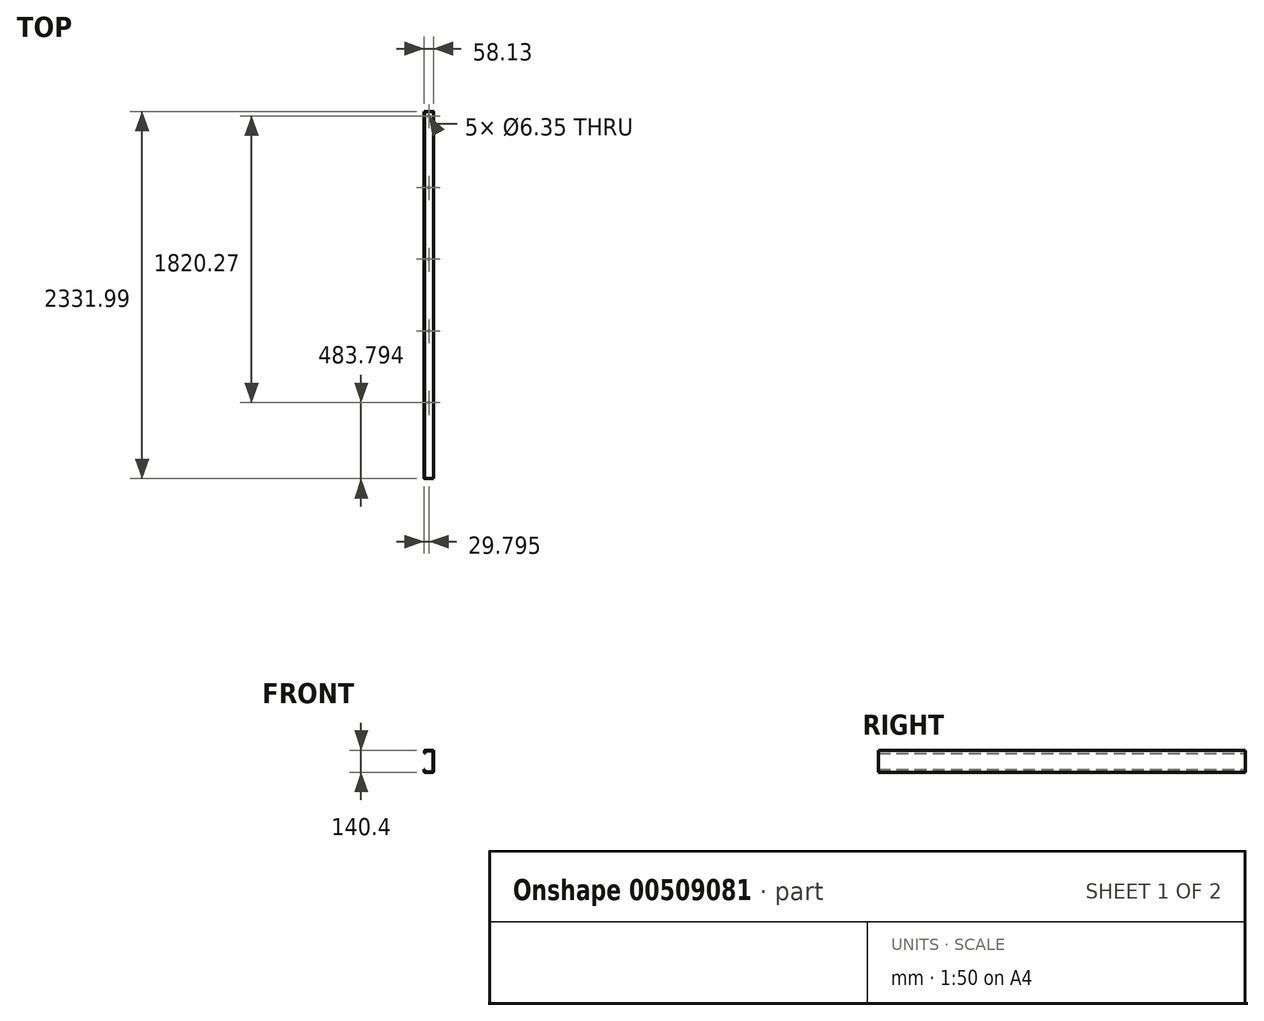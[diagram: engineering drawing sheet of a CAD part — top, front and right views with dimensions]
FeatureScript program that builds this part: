
annotation { "Feature Type Name" : "Feature", "Feature Type Description" : "" }
export const myFeature = defineFeature(function(context is Context, id is Id, definition is map)
    precondition{}
    {
        {
            var Q0;
            Q0=qCreatedBy(makeId("Front.planeOp"),FACE);
            var sketch = newSketch(context, id + "F0", { "sketchPlane" : qUnion([Q0])});
            skLineSegment(sketch, "E0", {"start": v(-431.8, -558.8) * mm, "end": v(431.8, -558.8) * mm});
            skLineSegment(sketch, "E1", {"start": v(431.8, -558.8) * mm, "end": v(431.8, 558.8) * mm});
            skLineSegment(sketch, "E2", {"start": v(431.8, 558.8) * mm, "end": v(-431.8, 558.8) * mm});
            skLineSegment(sketch, "E3", {"start": v(-431.8, 558.8) * mm, "end": v(-431.8, -558.8) * mm});
            skLineSegment(sketch, "E4", {"start": v(-381, -504.83) * mm, "end": v(381, -504.83) * mm});
            skLineSegment(sketch, "E5", {"start": v(381, -504.83) * mm, "end": v(381, 504.83) * mm});
            skLineSegment(sketch, "E6", {"start": v(381, 504.83) * mm, "end": v(360.7, 504.83) * mm});
            skLineSegment(sketch, "E7", {"start": v(265.82, 504.83) * mm, "end": v(-381, 504.83) * mm});
            skLineSegment(sketch, "E8", {"start": v(-381, 504.83) * mm, "end": v(-381, -504.83) * mm});
            skLineSegment(sketch, "E9", {"start": v(-381, -403.23) * mm, "end": v(381, -403.23) * mm});
            skLineSegment(sketch, "E10", {"start": v(-152.4, -403.23) * mm, "end": v(-152.4, -504.83) * mm});
            skLineSegment(sketch, "E11", {"start": v(152.4, -403.23) * mm, "end": v(152.4, -504.83) * mm});
            skLineSegment(sketch, "E12", {"start": v(349.12, 503.33) * mm, "end": v(324.77, 544.8) * mm});
            skLineSegment(sketch, "E13", {"start": v(324.92, 525.17) * mm, "end": v(343.26, 493.25) * mm});
            skLineSegment(sketch, "E14", {"start": v(345.3, 496.77) * mm, "end": v(323.11, 534.57) * mm});
            skLineSegment(sketch, "E15", {"start": v(351.17, 506.85) * mm, "end": v(327.06, 548.5) * mm});
            skLineSegment(sketch, "E16", {"start": v(335.24, 486.66) * mm, "end": v(339.43, 486.66) * mm});
            skLineSegment(sketch, "E17", {"start": v(323.53, 514.34) * mm, "end": v(339.43, 486.66) * mm});
            skLineSegment(sketch, "E18", {"start": v(324.77, 544.8) * mm, "end": v(303.2, 507.27) * mm});
            skLineSegment(sketch, "E19", {"start": v(323.11, 534.57) * mm, "end": v(305.2, 503.47) * mm});
            skLineSegment(sketch, "E20", {"start": v(303.02, 548.5) * mm, "end": v(279.32, 507.27) * mm});
            skLineSegment(sketch, "E21", {"start": v(305.2, 503.47) * mm, "end": v(281.51, 503.47) * mm});
            skLineSegment(sketch, "E22", {"start": v(303.2, 507.27) * mm, "end": v(279.32, 507.27) * mm});
            skLineSegment(sketch, "E23", {"start": v(287.46, 493.17) * mm, "end": v(311.53, 493.17) * mm});
            skLineSegment(sketch, "E24", {"start": v(285.48, 496.6) * mm, "end": v(309, 496.6) * mm});
            skLineSegment(sketch, "E25", {"start": v(315.3, 486.66) * mm, "end": v(291.22, 486.66) * mm});
            skLineSegment(sketch, "E26", {"start": v(281.51, 503.47) * mm, "end": v(285.48, 496.6) * mm});
            skLineSegment(sketch, "E27", {"start": v(287.46, 493.17) * mm, "end": v(291.22, 486.66) * mm});
            skLineSegment(sketch, "E28", {"start": v(309, 496.6) * mm, "end": v(324.92, 525.17) * mm});
            skLineSegment(sketch, "E29", {"start": v(311.53, 493.17) * mm, "end": v(323.53, 514.34) * mm});
            skLineSegment(sketch, "E30", {"start": v(325.28, 503.65) * mm, "end": v(315.3, 486.66) * mm});
            skLineSegment(sketch, "E31", {"start": v(319.7, 486.66) * mm, "end": v(326.89, 486.66) * mm});
            skLineSegment(sketch, "E32", {"start": v(319.7, 486.66) * mm, "end": v(323.3, 492.99) * mm});
            skLineSegment(sketch, "E33", {"start": v(335.24, 486.66) * mm, "end": v(325.28, 503.65) * mm});
            skLineSegment(sketch, "E34", {"start": v(323.3, 492.99) * mm, "end": v(326.89, 486.66) * mm});
            skLineSegment(sketch, "E35", {"start": v(327.06, 548.5) * mm, "end": v(303.02, 548.5) * mm});
            skLineSegment(sketch, "E36", {"start": v(343.26, 493.25) * mm, "end": v(345.3, 496.77) * mm});
            skLineSegment(sketch, "E37", {"start": v(349.12, 503.33) * mm, "end": v(351.17, 506.85) * mm});
            skCircle(sketch, "E38", {"center": v(350.6, 458.79) * mm, "radius": 1.85 * mm});
            skLineSegment(sketch, "E39", {"start": v(-201.65, 389.86) * mm, "end": v(-204.7, 389.86) * mm});
            skLineSegment(sketch, "E40", {"start": v(-201.65, 287.56) * mm, "end": v(-204.7, 287.56) * mm});
            skLineSegment(sketch, "E41", {"start": v(-204.7, 389.86) * mm, "end": v(-204.7, 405.1) * mm});
            skLineSegment(sketch, "E42", {"start": v(-201.65, 389.86) * mm, "end": v(-201.65, 405.1) * mm});
            skArc(sketch, "E43", {"start": v(-200.89, 405.86) * mm, "mid": v(-201.43, 405.64) * mm, "end": v(-201.65, 405.1) * mm});
            skArc(sketch, "E44", {"start": v(-200.89, 408.9) * mm, "mid": v(-203.58, 407.8) * mm, "end": v(-204.7, 405.1) * mm});
            skLineSegment(sketch, "E45", {"start": v(-200.89, 408.9) * mm, "end": v(-151.83, 408.9) * mm});
            skLineSegment(sketch, "E46", {"start": v(-200.89, 405.86) * mm, "end": v(-151.83, 405.86) * mm});
            skArc(sketch, "E47", {"start": v(-151.07, 405.1) * mm, "mid": v(-151.3, 405.64) * mm, "end": v(-151.83, 405.86) * mm});
            skArc(sketch, "E48", {"start": v(-148.02, 405.1) * mm, "mid": v(-149.14, 407.8) * mm, "end": v(-151.83, 408.9) * mm});
            skLineSegment(sketch, "E49", {"start": v(-148.02, 405.1) * mm, "end": v(-148.02, 272.32) * mm});
            skLineSegment(sketch, "E50", {"start": v(-151.07, 405.1) * mm, "end": v(-151.07, 272.32) * mm});
            skLineSegment(sketch, "E51", {"start": v(-204.7, 287.56) * mm, "end": v(-204.7, 273.15) * mm});
            skLineSegment(sketch, "E52", {"start": v(-201.65, 287.56) * mm, "end": v(-201.65, 273.15) * mm});
            skLineSegment(sketch, "E53", {"start": v(-200.06, 268.51) * mm, "end": v(-151.83, 268.51) * mm});
            skLineSegment(sketch, "E54", {"start": v(-200.06, 271.56) * mm, "end": v(-151.83, 271.56) * mm});
            skArc(sketch, "E55", {"start": v(-151.83, 271.56) * mm, "mid": v(-151.3, 271.79) * mm, "end": v(-151.07, 272.32) * mm});
            skArc(sketch, "E56", {"start": v(-151.83, 268.51) * mm, "mid": v(-149.14, 269.63) * mm, "end": v(-148.02, 272.32) * mm});
            skArc(sketch, "E57", {"start": v(-201.65, 273.15) * mm, "mid": v(-201.19, 272.03) * mm, "end": v(-200.06, 271.56) * mm});
            skArc(sketch, "E58", {"start": v(-204.7, 273.15) * mm, "mid": v(-203.34, 269.87) * mm, "end": v(-200.06, 268.51) * mm});
            skLineSegment(sketch, "E59", {"start": v(268.24, 192.18) * mm, "end": v(-275.4, 192.18) * mm});
            skLineSegment(sketch, "E60", {"start": v(-275.4, 267.58) * mm, "end": v(268.24, 267.58) * mm});
            skLineSegment(sketch, "E61", {"start": v(-275.4, 191.38) * mm, "end": v(268.24, 191.38) * mm});
            skLineSegment(sketch, "E62", {"start": v(-275.4, 189.56) * mm, "end": v(-275.4, 233.5) * mm});
            skLineSegment(sketch, "E63", {"start": v(-275.4, 238.46) * mm, "end": v(-275.4, 270.12) * mm});
            skLineSegment(sketch, "E64", {"start": v(-275.4, 233.5) * mm, "end": v(-264.27, 236) * mm});
            skLineSegment(sketch, "E65", {"start": v(-287.59, 236) * mm, "end": v(-275.4, 238.46) * mm});
            skLineSegment(sketch, "E66", {"start": v(-287.59, 236) * mm, "end": v(-264.27, 236) * mm});
            skLineSegment(sketch, "E67", {"start": v(268.24, 189.56) * mm, "end": v(268.24, 233.5) * mm});
            skLineSegment(sketch, "E68", {"start": v(268.24, 238.46) * mm, "end": v(268.24, 270.12) * mm});
            skLineSegment(sketch, "E69", {"start": v(268.24, 233.5) * mm, "end": v(279.38, 236) * mm});
            skLineSegment(sketch, "E70", {"start": v(256.06, 236) * mm, "end": v(268.24, 238.46) * mm});
            skLineSegment(sketch, "E71", {"start": v(256.06, 236) * mm, "end": v(279.38, 236) * mm});
            skLineSegment(sketch, "E72", {"start": v(267.92, 175.66) * mm, "end": v(267.92, 187.92) * mm});
            skLineSegment(sketch, "E73", {"start": v(-275.4, 175.66) * mm, "end": v(-275.4, 187.92) * mm});
            skLineSegment(sketch, "E74", {"start": v(131.2, 389.86) * mm, "end": v(128.15, 389.86) * mm});
            skLineSegment(sketch, "E75", {"start": v(131.2, 287.54) * mm, "end": v(128.15, 287.54) * mm});
            skLineSegment(sketch, "E76", {"start": v(128.15, 389.86) * mm, "end": v(128.15, 405.1) * mm});
            skLineSegment(sketch, "E77", {"start": v(131.2, 389.86) * mm, "end": v(131.2, 405.1) * mm});
            skArc(sketch, "E78", {"start": v(131.96, 408.9) * mm, "mid": v(129.27, 407.8) * mm, "end": v(128.15, 405.1) * mm});
            skLineSegment(sketch, "E79", {"start": v(131.96, 408.9) * mm, "end": v(182.96, 408.9) * mm});
            skLineSegment(sketch, "E80", {"start": v(131.96, 405.86) * mm, "end": v(182.96, 405.86) * mm});
            skArc(sketch, "E81", {"start": v(183.72, 405.1) * mm, "mid": v(183.5, 405.64) * mm, "end": v(182.96, 405.86) * mm});
            skArc(sketch, "E82", {"start": v(186.77, 405.1) * mm, "mid": v(185.65, 407.8) * mm, "end": v(182.96, 408.9) * mm});
            skLineSegment(sketch, "E83", {"start": v(186.77, 405.1) * mm, "end": v(186.77, 272.3) * mm});
            skLineSegment(sketch, "E84", {"start": v(183.72, 405.1) * mm, "end": v(183.72, 272.3) * mm});
            skLineSegment(sketch, "E85", {"start": v(128.15, 287.54) * mm, "end": v(128.15, 273.12) * mm});
            skLineSegment(sketch, "E86", {"start": v(131.2, 287.54) * mm, "end": v(131.2, 273.12) * mm});
            skLineSegment(sketch, "E87", {"start": v(132.79, 268.49) * mm, "end": v(182.96, 268.49) * mm});
            skLineSegment(sketch, "E88", {"start": v(132.79, 271.53) * mm, "end": v(182.96, 271.53) * mm});
            skArc(sketch, "E89", {"start": v(182.96, 271.53) * mm, "mid": v(183.5, 271.76) * mm, "end": v(183.72, 272.3) * mm});
            skArc(sketch, "E90", {"start": v(182.96, 268.49) * mm, "mid": v(185.65, 269.6) * mm, "end": v(186.77, 272.3) * mm});
            skArc(sketch, "E91", {"start": v(131.2, 273.12) * mm, "mid": v(131.67, 272) * mm, "end": v(132.79, 271.53) * mm});
            skArc(sketch, "E92", {"start": v(128.15, 273.12) * mm, "mid": v(129.51, 269.84) * mm, "end": v(132.79, 268.49) * mm});
            skLineSegment(sketch, "E93", {"start": v(-275.4, 266.78) * mm, "end": v(268.24, 266.78) * mm});
            skArc(sketch, "E94", {"start": v(131.96, 405.86) * mm, "mid": v(131.42, 405.64) * mm, "end": v(131.2, 405.1) * mm});
            skLineSegment(sketch, "E95", {"start": v(-148.02, 350.55) * mm, "end": v(-147.38, 350.55) * mm});
            skLineSegment(sketch, "E96", {"start": v(268.24, 220.63) * mm, "end": v(-275.4, 220.63) * mm});
            skLineSegment(sketch, "E97", {"start": v(-275.4, 219.83) * mm, "end": v(268.24, 219.83) * mm});
            skLineSegment(sketch, "E98", {"start": v(111.4, 219.88) * mm, "end": v(200.2, 219.88) * mm});
            skLineSegment(sketch, "E99", {"start": v(200.2, 219.88) * mm, "end": v(200.2, 218.1) * mm});
            skLineSegment(sketch, "E100", {"start": v(111.4, 219.88) * mm, "end": v(111.4, 218.1) * mm});
            skLineSegment(sketch, "E101", {"start": v(111.4, 218.1) * mm, "end": v(200.2, 218.1) * mm});
            skLineSegment(sketch, "E102", {"start": v(165.87, 216.24) * mm, "end": v(165.87, 217.5) * mm});
            skLineSegment(sketch, "E103", {"start": v(152.66, 216.24) * mm, "end": v(152.66, 217.5) * mm});
            skLineSegment(sketch, "E104", {"start": v(164.46, 211.81) * mm, "end": v(164.46, 216.24) * mm});
            skLineSegment(sketch, "E105", {"start": v(154.07, 211.81) * mm, "end": v(154.07, 216.24) * mm});
            skLineSegment(sketch, "E106", {"start": v(161.7, 259.32) * mm, "end": v(161.7, 260.34) * mm});
            skLineSegment(sketch, "E107", {"start": v(161.7, 261.14) * mm, "end": v(161.7, 262.16) * mm});
            skLineSegment(sketch, "E108", {"start": v(161.7, 262.95) * mm, "end": v(161.7, 263.97) * mm});
            skLineSegment(sketch, "E109", {"start": v(161.7, 264.76) * mm, "end": v(161.7, 265.78) * mm});
            skLineSegment(sketch, "E110", {"start": v(161.7, 266.58) * mm, "end": v(161.7, 267.6) * mm});
            skLineSegment(sketch, "E111", {"start": v(161.7, 268.39) * mm, "end": v(161.7, 269.41) * mm});
            skLineSegment(sketch, "E112", {"start": v(161.7, 270.2) * mm, "end": v(161.7, 271.22) * mm});
            skLineSegment(sketch, "E113", {"start": v(161.7, 272.02) * mm, "end": v(161.7, 273.04) * mm});
            skLineSegment(sketch, "E114", {"start": v(161.7, 273.83) * mm, "end": v(161.7, 274.85) * mm});
            skLineSegment(sketch, "E115", {"start": v(161.7, 275.64) * mm, "end": v(161.7, 276.67) * mm});
            skLineSegment(sketch, "E116", {"start": v(161.7, 277.46) * mm, "end": v(161.7, 278.48) * mm});
            skLineSegment(sketch, "E117", {"start": v(156.83, 257.5) * mm, "end": v(156.83, 258.53) * mm});
            skLineSegment(sketch, "E118", {"start": v(156.83, 259.32) * mm, "end": v(156.83, 260.34) * mm});
            skLineSegment(sketch, "E119", {"start": v(156.83, 261.14) * mm, "end": v(156.83, 262.16) * mm});
            skLineSegment(sketch, "E120", {"start": v(156.83, 262.95) * mm, "end": v(156.83, 263.97) * mm});
            skLineSegment(sketch, "E121", {"start": v(156.83, 264.76) * mm, "end": v(156.83, 265.78) * mm});
            skLineSegment(sketch, "E122", {"start": v(156.83, 266.58) * mm, "end": v(156.83, 267.6) * mm});
            skLineSegment(sketch, "E123", {"start": v(156.83, 268.39) * mm, "end": v(156.83, 269.41) * mm});
            skLineSegment(sketch, "E124", {"start": v(156.83, 270.2) * mm, "end": v(156.83, 271.22) * mm});
            skLineSegment(sketch, "E125", {"start": v(156.83, 272.02) * mm, "end": v(156.83, 273.04) * mm});
            skLineSegment(sketch, "E126", {"start": v(156.83, 273.83) * mm, "end": v(156.83, 274.85) * mm});
            skLineSegment(sketch, "E127", {"start": v(156.83, 275.64) * mm, "end": v(156.83, 276.67) * mm});
            skLineSegment(sketch, "E128", {"start": v(156.14, 258.93) * mm, "end": v(156.83, 258.53) * mm});
            skLineSegment(sketch, "E129", {"start": v(156.14, 258.93) * mm, "end": v(156.83, 259.32) * mm});
            skLineSegment(sketch, "E130", {"start": v(156.14, 260.74) * mm, "end": v(156.83, 260.34) * mm});
            skLineSegment(sketch, "E131", {"start": v(156.14, 260.74) * mm, "end": v(156.83, 261.14) * mm});
            skLineSegment(sketch, "E132", {"start": v(162.39, 260.74) * mm, "end": v(161.7, 260.34) * mm});
            skLineSegment(sketch, "E133", {"start": v(162.39, 260.74) * mm, "end": v(161.7, 261.14) * mm});
            skLineSegment(sketch, "E134", {"start": v(162.39, 262.55) * mm, "end": v(161.7, 262.16) * mm});
            skLineSegment(sketch, "E135", {"start": v(162.39, 262.55) * mm, "end": v(161.7, 262.95) * mm});
            skLineSegment(sketch, "E136", {"start": v(156.14, 258.93) * mm, "end": v(162.39, 260.74) * mm});
            skLineSegment(sketch, "E137", {"start": v(156.14, 260.74) * mm, "end": v(162.39, 262.55) * mm});
            skLineSegment(sketch, "E138", {"start": v(156.83, 258.53) * mm, "end": v(161.7, 260.34) * mm});
            skLineSegment(sketch, "E139", {"start": v(156.83, 259.32) * mm, "end": v(161.7, 261.14) * mm});
            skLineSegment(sketch, "E140", {"start": v(156.83, 260.34) * mm, "end": v(161.7, 262.16) * mm});
            skLineSegment(sketch, "E141", {"start": v(156.83, 261.14) * mm, "end": v(161.7, 262.95) * mm});
            skLineSegment(sketch, "E142", {"start": v(156.14, 262.55) * mm, "end": v(156.83, 262.16) * mm});
            skLineSegment(sketch, "E143", {"start": v(156.14, 262.55) * mm, "end": v(156.83, 262.95) * mm});
            skLineSegment(sketch, "E144", {"start": v(156.14, 264.37) * mm, "end": v(156.83, 263.97) * mm});
            skLineSegment(sketch, "E145", {"start": v(156.14, 264.37) * mm, "end": v(156.83, 264.76) * mm});
            skLineSegment(sketch, "E146", {"start": v(162.39, 264.37) * mm, "end": v(161.7, 263.97) * mm});
            skLineSegment(sketch, "E147", {"start": v(162.39, 264.37) * mm, "end": v(161.7, 264.76) * mm});
            skLineSegment(sketch, "E148", {"start": v(162.39, 266.18) * mm, "end": v(161.7, 265.78) * mm});
            skLineSegment(sketch, "E149", {"start": v(162.39, 266.18) * mm, "end": v(161.7, 266.58) * mm});
            skLineSegment(sketch, "E150", {"start": v(156.14, 262.55) * mm, "end": v(162.39, 264.37) * mm});
            skLineSegment(sketch, "E151", {"start": v(156.14, 264.37) * mm, "end": v(162.39, 266.18) * mm});
            skLineSegment(sketch, "E152", {"start": v(156.83, 262.16) * mm, "end": v(161.7, 263.97) * mm});
            skLineSegment(sketch, "E153", {"start": v(156.83, 262.95) * mm, "end": v(161.7, 264.76) * mm});
            skLineSegment(sketch, "E154", {"start": v(156.83, 263.97) * mm, "end": v(161.7, 265.78) * mm});
            skLineSegment(sketch, "E155", {"start": v(156.83, 264.76) * mm, "end": v(161.7, 266.58) * mm});
            skLineSegment(sketch, "E156", {"start": v(156.14, 266.18) * mm, "end": v(156.83, 265.78) * mm});
            skLineSegment(sketch, "E157", {"start": v(156.14, 266.18) * mm, "end": v(156.83, 266.58) * mm});
            skLineSegment(sketch, "E158", {"start": v(162.39, 268) * mm, "end": v(161.7, 267.6) * mm});
            skLineSegment(sketch, "E159", {"start": v(162.39, 268) * mm, "end": v(161.7, 268.39) * mm});
            skLineSegment(sketch, "E160", {"start": v(156.14, 266.18) * mm, "end": v(162.39, 268) * mm});
            skLineSegment(sketch, "E161", {"start": v(156.83, 265.78) * mm, "end": v(161.7, 267.6) * mm});
            skLineSegment(sketch, "E162", {"start": v(156.83, 266.58) * mm, "end": v(161.7, 268.39) * mm});
            skLineSegment(sketch, "E163", {"start": v(156.14, 268) * mm, "end": v(156.83, 267.6) * mm});
            skLineSegment(sketch, "E164", {"start": v(156.14, 268) * mm, "end": v(156.83, 268.39) * mm});
            skLineSegment(sketch, "E165", {"start": v(156.14, 269.8) * mm, "end": v(156.83, 269.41) * mm});
            skLineSegment(sketch, "E166", {"start": v(156.14, 269.8) * mm, "end": v(156.83, 270.2) * mm});
            skLineSegment(sketch, "E167", {"start": v(162.39, 269.8) * mm, "end": v(161.7, 269.41) * mm});
            skLineSegment(sketch, "E168", {"start": v(162.39, 269.8) * mm, "end": v(161.7, 270.2) * mm});
            skLineSegment(sketch, "E169", {"start": v(162.39, 271.62) * mm, "end": v(161.7, 271.22) * mm});
            skLineSegment(sketch, "E170", {"start": v(162.39, 271.62) * mm, "end": v(161.7, 272.02) * mm});
            skLineSegment(sketch, "E171", {"start": v(156.14, 268) * mm, "end": v(162.39, 269.8) * mm});
            skLineSegment(sketch, "E172", {"start": v(156.14, 269.8) * mm, "end": v(162.39, 271.62) * mm});
            skLineSegment(sketch, "E173", {"start": v(156.83, 267.6) * mm, "end": v(161.7, 269.41) * mm});
            skLineSegment(sketch, "E174", {"start": v(156.83, 268.39) * mm, "end": v(161.7, 270.2) * mm});
            skLineSegment(sketch, "E175", {"start": v(156.83, 269.41) * mm, "end": v(161.7, 271.22) * mm});
            skLineSegment(sketch, "E176", {"start": v(156.83, 270.2) * mm, "end": v(161.7, 272.02) * mm});
            skLineSegment(sketch, "E177", {"start": v(156.14, 271.62) * mm, "end": v(156.83, 271.22) * mm});
            skLineSegment(sketch, "E178", {"start": v(156.14, 271.62) * mm, "end": v(156.83, 272.02) * mm});
            skLineSegment(sketch, "E179", {"start": v(156.14, 273.43) * mm, "end": v(156.83, 273.04) * mm});
            skLineSegment(sketch, "E180", {"start": v(156.14, 273.43) * mm, "end": v(156.83, 273.83) * mm});
            skLineSegment(sketch, "E181", {"start": v(162.39, 273.43) * mm, "end": v(161.7, 273.04) * mm});
            skLineSegment(sketch, "E182", {"start": v(162.39, 273.43) * mm, "end": v(161.7, 273.83) * mm});
            skLineSegment(sketch, "E183", {"start": v(162.39, 275.25) * mm, "end": v(161.7, 274.85) * mm});
            skLineSegment(sketch, "E184", {"start": v(162.39, 275.25) * mm, "end": v(161.7, 275.64) * mm});
            skLineSegment(sketch, "E185", {"start": v(156.14, 271.62) * mm, "end": v(162.39, 273.43) * mm});
            skLineSegment(sketch, "E186", {"start": v(156.14, 273.43) * mm, "end": v(162.39, 275.25) * mm});
            skLineSegment(sketch, "E187", {"start": v(156.83, 271.22) * mm, "end": v(161.7, 273.04) * mm});
            skLineSegment(sketch, "E188", {"start": v(156.83, 272.02) * mm, "end": v(161.7, 273.83) * mm});
            skLineSegment(sketch, "E189", {"start": v(156.83, 273.04) * mm, "end": v(161.7, 274.85) * mm});
            skLineSegment(sketch, "E190", {"start": v(156.83, 273.83) * mm, "end": v(161.7, 275.64) * mm});
            skLineSegment(sketch, "E191", {"start": v(156.14, 275.25) * mm, "end": v(156.83, 274.85) * mm});
            skLineSegment(sketch, "E192", {"start": v(156.14, 275.25) * mm, "end": v(156.83, 275.64) * mm});
            skLineSegment(sketch, "E193", {"start": v(156.14, 277.06) * mm, "end": v(156.83, 276.67) * mm});
            skLineSegment(sketch, "E194", {"start": v(156.14, 277.06) * mm, "end": v(156.83, 277.46) * mm});
            skLineSegment(sketch, "E195", {"start": v(162.39, 277.06) * mm, "end": v(161.7, 276.67) * mm});
            skLineSegment(sketch, "E196", {"start": v(162.39, 277.06) * mm, "end": v(161.7, 277.46) * mm});
            skLineSegment(sketch, "E197", {"start": v(162.39, 278.87) * mm, "end": v(161.7, 278.48) * mm});
            skLineSegment(sketch, "E198", {"start": v(162.39, 278.87) * mm, "end": v(161.7, 279.27) * mm});
            skLineSegment(sketch, "E199", {"start": v(156.14, 275.25) * mm, "end": v(162.39, 277.06) * mm});
            skLineSegment(sketch, "E200", {"start": v(156.14, 277.06) * mm, "end": v(162.39, 278.87) * mm});
            skLineSegment(sketch, "E201", {"start": v(156.83, 274.85) * mm, "end": v(161.7, 276.67) * mm});
            skLineSegment(sketch, "E202", {"start": v(156.83, 275.64) * mm, "end": v(161.7, 277.46) * mm});
            skLineSegment(sketch, "E203", {"start": v(156.83, 276.67) * mm, "end": v(161.7, 278.48) * mm});
            skLineSegment(sketch, "E204", {"start": v(156.83, 277.46) * mm, "end": v(161.7, 279.27) * mm});
            skLineSegment(sketch, "E205", {"start": v(152.66, 217.5) * mm, "end": v(165.87, 217.5) * mm});
            skLineSegment(sketch, "E206", {"start": v(152.66, 216.24) * mm, "end": v(165.87, 216.24) * mm});
            skLineSegment(sketch, "E207", {"start": v(154.77, 211.41) * mm, "end": v(163.76, 211.41) * mm});
            skLineSegment(sketch, "E208", {"start": v(156.67, 211.81) * mm, "end": v(156.67, 216.24) * mm});
            skLineSegment(sketch, "E209", {"start": v(161.86, 211.81) * mm, "end": v(161.86, 216.24) * mm});
            skLineSegment(sketch, "E210", {"start": v(154.77, 211.41) * mm, "end": v(154.07, 211.81) * mm});
            skLineSegment(sketch, "E211", {"start": v(163.76, 211.41) * mm, "end": v(164.46, 211.81) * mm});
            skLineSegment(sketch, "E212", {"start": v(161.16, 211.41) * mm, "end": v(161.86, 211.81) * mm});
            skLineSegment(sketch, "E213", {"start": v(155.97, 211.41) * mm, "end": v(156.67, 211.81) * mm});
            skLineSegment(sketch, "E214", {"start": v(162.56, 211.41) * mm, "end": v(161.86, 211.81) * mm});
            skLineSegment(sketch, "E215", {"start": v(157.36, 211.41) * mm, "end": v(156.67, 211.81) * mm});
            skLineSegment(sketch, "E216", {"start": v(156.83, 277.46) * mm, "end": v(156.83, 288.94) * mm});
            skLineSegment(sketch, "E217", {"start": v(161.05, 279.03) * mm, "end": v(161.05, 288.94) * mm});
            skLineSegment(sketch, "E218", {"start": v(158.94, 290.16) * mm, "end": v(156.83, 288.94) * mm});
            skLineSegment(sketch, "E219", {"start": v(158.94, 290.16) * mm, "end": v(161.05, 288.94) * mm});
            skLineSegment(sketch, "E220", {"start": v(158.94, 290.16) * mm, "end": v(158.94, 280.63) * mm});
            skArc(sketch, "E221", {"start": v(158.94, 280.63) * mm, "mid": v(159.28, 279.49) * mm, "end": v(160.18, 278.7) * mm});
            skLineSegment(sketch, "E222", {"start": v(156.14, 257.11) * mm, "end": v(156.83, 256.72) * mm});
            skLineSegment(sketch, "E223", {"start": v(156.14, 257.11) * mm, "end": v(156.83, 257.5) * mm});
            skLineSegment(sketch, "E224", {"start": v(162.39, 258.93) * mm, "end": v(161.7, 258.53) * mm});
            skLineSegment(sketch, "E225", {"start": v(162.39, 258.93) * mm, "end": v(161.7, 259.32) * mm});
            skLineSegment(sketch, "E226", {"start": v(156.14, 257.11) * mm, "end": v(162.39, 258.93) * mm});
            skLineSegment(sketch, "E227", {"start": v(156.83, 256.72) * mm, "end": v(161.7, 258.53) * mm});
            skLineSegment(sketch, "E228", {"start": v(156.83, 257.5) * mm, "end": v(161.7, 259.32) * mm});
            skLineSegment(sketch, "E229", {"start": v(156.83, 256.72) * mm, "end": v(156.83, 217.5) * mm});
            skLineSegment(sketch, "E230", {"start": v(161.7, 258.53) * mm, "end": v(161.7, 217.5) * mm});
            skLineSegment(sketch, "E231", {"start": v(-224.84, 219.88) * mm, "end": v(-136.05, 219.88) * mm});
            skLineSegment(sketch, "E232", {"start": v(-224.84, 218.1) * mm, "end": v(-136.05, 218.1) * mm});
            skLineSegment(sketch, "E233", {"start": v(-136.05, 219.88) * mm, "end": v(-136.05, 218.1) * mm});
            skLineSegment(sketch, "E234", {"start": v(-224.84, 219.88) * mm, "end": v(-224.84, 218.1) * mm});
            skLineSegment(sketch, "E235", {"start": v(-170.37, 216.24) * mm, "end": v(-170.37, 217.5) * mm});
            skLineSegment(sketch, "E236", {"start": v(-183.58, 216.24) * mm, "end": v(-183.58, 217.5) * mm});
            skLineSegment(sketch, "E237", {"start": v(-171.78, 211.81) * mm, "end": v(-171.78, 216.24) * mm});
            skLineSegment(sketch, "E238", {"start": v(-182.17, 211.81) * mm, "end": v(-182.17, 216.24) * mm});
            skLineSegment(sketch, "E239", {"start": v(-174.54, 259.32) * mm, "end": v(-174.54, 260.34) * mm});
            skLineSegment(sketch, "E240", {"start": v(-174.54, 261.14) * mm, "end": v(-174.54, 262.16) * mm});
            skLineSegment(sketch, "E241", {"start": v(-174.54, 262.95) * mm, "end": v(-174.54, 263.97) * mm});
            skLineSegment(sketch, "E242", {"start": v(-174.54, 264.76) * mm, "end": v(-174.54, 265.78) * mm});
            skLineSegment(sketch, "E243", {"start": v(-174.54, 266.58) * mm, "end": v(-174.54, 267.6) * mm});
            skLineSegment(sketch, "E244", {"start": v(-174.54, 268.39) * mm, "end": v(-174.54, 269.41) * mm});
            skLineSegment(sketch, "E245", {"start": v(-174.54, 270.2) * mm, "end": v(-174.54, 271.22) * mm});
            skLineSegment(sketch, "E246", {"start": v(-174.54, 272.02) * mm, "end": v(-174.54, 273.04) * mm});
            skLineSegment(sketch, "E247", {"start": v(-174.54, 273.83) * mm, "end": v(-174.54, 274.85) * mm});
            skLineSegment(sketch, "E248", {"start": v(-174.54, 275.64) * mm, "end": v(-174.54, 276.67) * mm});
            skLineSegment(sketch, "E249", {"start": v(-174.54, 277.46) * mm, "end": v(-174.54, 278.48) * mm});
            skLineSegment(sketch, "E250", {"start": v(-179.41, 257.5) * mm, "end": v(-179.41, 258.53) * mm});
            skLineSegment(sketch, "E251", {"start": v(-179.41, 259.32) * mm, "end": v(-179.41, 260.34) * mm});
            skLineSegment(sketch, "E252", {"start": v(-179.41, 261.14) * mm, "end": v(-179.41, 262.16) * mm});
            skLineSegment(sketch, "E253", {"start": v(-179.41, 262.95) * mm, "end": v(-179.41, 263.97) * mm});
            skLineSegment(sketch, "E254", {"start": v(-179.41, 264.76) * mm, "end": v(-179.41, 265.78) * mm});
            skLineSegment(sketch, "E255", {"start": v(-179.41, 266.58) * mm, "end": v(-179.41, 267.6) * mm});
            skLineSegment(sketch, "E256", {"start": v(-179.41, 268.39) * mm, "end": v(-179.41, 269.41) * mm});
            skLineSegment(sketch, "E257", {"start": v(-179.41, 270.2) * mm, "end": v(-179.41, 271.22) * mm});
            skLineSegment(sketch, "E258", {"start": v(-179.41, 272.02) * mm, "end": v(-179.41, 273.04) * mm});
            skLineSegment(sketch, "E259", {"start": v(-179.41, 273.83) * mm, "end": v(-179.41, 274.85) * mm});
            skLineSegment(sketch, "E260", {"start": v(-179.41, 275.64) * mm, "end": v(-179.41, 276.67) * mm});
            skLineSegment(sketch, "E261", {"start": v(-180.1, 258.93) * mm, "end": v(-179.41, 258.53) * mm});
            skLineSegment(sketch, "E262", {"start": v(-180.1, 258.93) * mm, "end": v(-179.41, 259.32) * mm});
            skLineSegment(sketch, "E263", {"start": v(-180.1, 260.74) * mm, "end": v(-179.41, 260.34) * mm});
            skLineSegment(sketch, "E264", {"start": v(-180.1, 260.74) * mm, "end": v(-179.41, 261.14) * mm});
            skLineSegment(sketch, "E265", {"start": v(-173.85, 260.74) * mm, "end": v(-174.54, 260.34) * mm});
            skLineSegment(sketch, "E266", {"start": v(-173.85, 260.74) * mm, "end": v(-174.54, 261.14) * mm});
            skLineSegment(sketch, "E267", {"start": v(-173.85, 262.55) * mm, "end": v(-174.54, 262.16) * mm});
            skLineSegment(sketch, "E268", {"start": v(-173.85, 262.55) * mm, "end": v(-174.54, 262.95) * mm});
            skLineSegment(sketch, "E269", {"start": v(-180.1, 258.93) * mm, "end": v(-173.85, 260.74) * mm});
            skLineSegment(sketch, "E270", {"start": v(-180.1, 260.74) * mm, "end": v(-173.85, 262.55) * mm});
            skLineSegment(sketch, "E271", {"start": v(-179.41, 258.53) * mm, "end": v(-174.54, 260.34) * mm});
            skLineSegment(sketch, "E272", {"start": v(-179.41, 259.32) * mm, "end": v(-174.54, 261.14) * mm});
            skLineSegment(sketch, "E273", {"start": v(-179.41, 260.34) * mm, "end": v(-174.54, 262.16) * mm});
            skLineSegment(sketch, "E274", {"start": v(-179.41, 261.14) * mm, "end": v(-174.54, 262.95) * mm});
            skLineSegment(sketch, "E275", {"start": v(-180.1, 262.55) * mm, "end": v(-179.41, 262.16) * mm});
            skLineSegment(sketch, "E276", {"start": v(-180.1, 262.55) * mm, "end": v(-179.41, 262.95) * mm});
            skLineSegment(sketch, "E277", {"start": v(-180.1, 264.37) * mm, "end": v(-179.41, 263.97) * mm});
            skLineSegment(sketch, "E278", {"start": v(-180.1, 264.37) * mm, "end": v(-179.41, 264.76) * mm});
            skLineSegment(sketch, "E279", {"start": v(-173.85, 264.37) * mm, "end": v(-174.54, 263.97) * mm});
            skLineSegment(sketch, "E280", {"start": v(-173.85, 264.37) * mm, "end": v(-174.54, 264.76) * mm});
            skLineSegment(sketch, "E281", {"start": v(-173.85, 266.18) * mm, "end": v(-174.54, 265.78) * mm});
            skLineSegment(sketch, "E282", {"start": v(-173.85, 266.18) * mm, "end": v(-174.54, 266.58) * mm});
            skLineSegment(sketch, "E283", {"start": v(-180.1, 262.55) * mm, "end": v(-173.85, 264.37) * mm});
            skLineSegment(sketch, "E284", {"start": v(-180.1, 264.37) * mm, "end": v(-173.85, 266.18) * mm});
            skLineSegment(sketch, "E285", {"start": v(-179.41, 262.16) * mm, "end": v(-174.54, 263.97) * mm});
            skLineSegment(sketch, "E286", {"start": v(-179.41, 262.95) * mm, "end": v(-174.54, 264.76) * mm});
            skLineSegment(sketch, "E287", {"start": v(-179.41, 263.97) * mm, "end": v(-174.54, 265.78) * mm});
            skLineSegment(sketch, "E288", {"start": v(-179.41, 264.76) * mm, "end": v(-174.54, 266.58) * mm});
            skLineSegment(sketch, "E289", {"start": v(-180.1, 266.18) * mm, "end": v(-179.41, 265.78) * mm});
            skLineSegment(sketch, "E290", {"start": v(-180.1, 266.18) * mm, "end": v(-179.41, 266.58) * mm});
            skLineSegment(sketch, "E291", {"start": v(-173.85, 268) * mm, "end": v(-174.54, 267.6) * mm});
            skLineSegment(sketch, "E292", {"start": v(-173.85, 268) * mm, "end": v(-174.54, 268.39) * mm});
            skLineSegment(sketch, "E293", {"start": v(-180.1, 266.18) * mm, "end": v(-173.85, 268) * mm});
            skLineSegment(sketch, "E294", {"start": v(-179.41, 265.78) * mm, "end": v(-174.54, 267.6) * mm});
            skLineSegment(sketch, "E295", {"start": v(-179.41, 266.58) * mm, "end": v(-174.54, 268.39) * mm});
            skLineSegment(sketch, "E296", {"start": v(-180.1, 268) * mm, "end": v(-179.41, 267.6) * mm});
            skLineSegment(sketch, "E297", {"start": v(-180.1, 268) * mm, "end": v(-179.41, 268.39) * mm});
            skLineSegment(sketch, "E298", {"start": v(-180.1, 269.8) * mm, "end": v(-179.41, 269.41) * mm});
            skLineSegment(sketch, "E299", {"start": v(-180.1, 269.8) * mm, "end": v(-179.41, 270.2) * mm});
            skLineSegment(sketch, "E300", {"start": v(-173.85, 269.8) * mm, "end": v(-174.54, 269.41) * mm});
            skLineSegment(sketch, "E301", {"start": v(-173.85, 269.8) * mm, "end": v(-174.54, 270.2) * mm});
            skLineSegment(sketch, "E302", {"start": v(-173.85, 271.62) * mm, "end": v(-174.54, 271.22) * mm});
            skLineSegment(sketch, "E303", {"start": v(-173.85, 271.62) * mm, "end": v(-174.54, 272.02) * mm});
            skLineSegment(sketch, "E304", {"start": v(-180.1, 268) * mm, "end": v(-173.85, 269.8) * mm});
            skLineSegment(sketch, "E305", {"start": v(-180.1, 269.8) * mm, "end": v(-173.85, 271.62) * mm});
            skLineSegment(sketch, "E306", {"start": v(-179.41, 267.6) * mm, "end": v(-174.54, 269.41) * mm});
            skLineSegment(sketch, "E307", {"start": v(-179.41, 268.39) * mm, "end": v(-174.54, 270.2) * mm});
            skLineSegment(sketch, "E308", {"start": v(-179.41, 269.41) * mm, "end": v(-174.54, 271.22) * mm});
            skLineSegment(sketch, "E309", {"start": v(-179.41, 270.2) * mm, "end": v(-174.54, 272.02) * mm});
            skLineSegment(sketch, "E310", {"start": v(-180.1, 271.62) * mm, "end": v(-179.41, 271.22) * mm});
            skLineSegment(sketch, "E311", {"start": v(-180.1, 271.62) * mm, "end": v(-179.41, 272.02) * mm});
            skLineSegment(sketch, "E312", {"start": v(-180.1, 273.43) * mm, "end": v(-179.41, 273.04) * mm});
            skLineSegment(sketch, "E313", {"start": v(-180.1, 273.43) * mm, "end": v(-179.41, 273.83) * mm});
            skLineSegment(sketch, "E314", {"start": v(-173.85, 273.43) * mm, "end": v(-174.54, 273.04) * mm});
            skLineSegment(sketch, "E315", {"start": v(-173.85, 273.43) * mm, "end": v(-174.54, 273.83) * mm});
            skLineSegment(sketch, "E316", {"start": v(-173.85, 275.25) * mm, "end": v(-174.54, 274.85) * mm});
            skLineSegment(sketch, "E317", {"start": v(-173.85, 275.25) * mm, "end": v(-174.54, 275.64) * mm});
            skLineSegment(sketch, "E318", {"start": v(-180.1, 271.62) * mm, "end": v(-173.85, 273.43) * mm});
            skLineSegment(sketch, "E319", {"start": v(-180.1, 273.43) * mm, "end": v(-173.85, 275.25) * mm});
            skLineSegment(sketch, "E320", {"start": v(-179.41, 271.22) * mm, "end": v(-174.54, 273.04) * mm});
            skLineSegment(sketch, "E321", {"start": v(-179.41, 272.02) * mm, "end": v(-174.54, 273.83) * mm});
            skLineSegment(sketch, "E322", {"start": v(-179.41, 273.04) * mm, "end": v(-174.54, 274.85) * mm});
            skLineSegment(sketch, "E323", {"start": v(-179.41, 273.83) * mm, "end": v(-174.54, 275.64) * mm});
            skLineSegment(sketch, "E324", {"start": v(-180.1, 275.25) * mm, "end": v(-179.41, 274.85) * mm});
            skLineSegment(sketch, "E325", {"start": v(-180.1, 275.25) * mm, "end": v(-179.41, 275.64) * mm});
            skLineSegment(sketch, "E326", {"start": v(-180.1, 277.06) * mm, "end": v(-179.41, 276.67) * mm});
            skLineSegment(sketch, "E327", {"start": v(-180.1, 277.06) * mm, "end": v(-179.41, 277.46) * mm});
            skLineSegment(sketch, "E328", {"start": v(-173.85, 277.06) * mm, "end": v(-174.54, 276.67) * mm});
            skLineSegment(sketch, "E329", {"start": v(-173.85, 277.06) * mm, "end": v(-174.54, 277.46) * mm});
            skLineSegment(sketch, "E330", {"start": v(-173.85, 278.87) * mm, "end": v(-174.54, 278.48) * mm});
            skLineSegment(sketch, "E331", {"start": v(-173.85, 278.87) * mm, "end": v(-174.54, 279.27) * mm});
            skLineSegment(sketch, "E332", {"start": v(-180.1, 275.25) * mm, "end": v(-173.85, 277.06) * mm});
            skLineSegment(sketch, "E333", {"start": v(-180.1, 277.06) * mm, "end": v(-173.85, 278.87) * mm});
            skLineSegment(sketch, "E334", {"start": v(-179.41, 274.85) * mm, "end": v(-174.54, 276.67) * mm});
            skLineSegment(sketch, "E335", {"start": v(-179.41, 275.64) * mm, "end": v(-174.54, 277.46) * mm});
            skLineSegment(sketch, "E336", {"start": v(-179.41, 276.67) * mm, "end": v(-174.54, 278.48) * mm});
            skLineSegment(sketch, "E337", {"start": v(-179.41, 277.46) * mm, "end": v(-174.54, 279.27) * mm});
            skLineSegment(sketch, "E338", {"start": v(-183.58, 217.5) * mm, "end": v(-170.37, 217.5) * mm});
            skLineSegment(sketch, "E339", {"start": v(-183.58, 216.24) * mm, "end": v(-170.37, 216.24) * mm});
            skLineSegment(sketch, "E340", {"start": v(-181.47, 211.41) * mm, "end": v(-172.48, 211.41) * mm});
            skLineSegment(sketch, "E341", {"start": v(-179.57, 211.81) * mm, "end": v(-179.57, 216.24) * mm});
            skLineSegment(sketch, "E342", {"start": v(-174.38, 211.81) * mm, "end": v(-174.38, 216.24) * mm});
            skLineSegment(sketch, "E343", {"start": v(-181.47, 211.41) * mm, "end": v(-182.17, 211.81) * mm});
            skLineSegment(sketch, "E344", {"start": v(-172.48, 211.41) * mm, "end": v(-171.78, 211.81) * mm});
            skLineSegment(sketch, "E345", {"start": v(-175.07, 211.41) * mm, "end": v(-174.38, 211.81) * mm});
            skLineSegment(sketch, "E346", {"start": v(-180.27, 211.41) * mm, "end": v(-179.57, 211.81) * mm});
            skLineSegment(sketch, "E347", {"start": v(-173.68, 211.41) * mm, "end": v(-174.38, 211.81) * mm});
            skLineSegment(sketch, "E348", {"start": v(-178.88, 211.41) * mm, "end": v(-179.57, 211.81) * mm});
            skLineSegment(sketch, "E349", {"start": v(-179.41, 277.46) * mm, "end": v(-179.41, 288.94) * mm});
            skLineSegment(sketch, "E350", {"start": v(-175.19, 279.03) * mm, "end": v(-175.19, 288.94) * mm});
            skLineSegment(sketch, "E351", {"start": v(-177.3, 290.16) * mm, "end": v(-179.41, 288.94) * mm});
            skLineSegment(sketch, "E352", {"start": v(-177.3, 290.16) * mm, "end": v(-175.19, 288.94) * mm});
            skLineSegment(sketch, "E353", {"start": v(-177.3, 290.16) * mm, "end": v(-177.3, 280.63) * mm});
            skArc(sketch, "E354", {"start": v(-177.3, 280.63) * mm, "mid": v(-176.96, 279.49) * mm, "end": v(-176.05, 278.7) * mm});
            skLineSegment(sketch, "E355", {"start": v(-180.1, 257.11) * mm, "end": v(-179.41, 256.72) * mm});
            skLineSegment(sketch, "E356", {"start": v(-180.1, 257.11) * mm, "end": v(-179.41, 257.5) * mm});
            skLineSegment(sketch, "E357", {"start": v(-173.85, 258.93) * mm, "end": v(-174.54, 258.53) * mm});
            skLineSegment(sketch, "E358", {"start": v(-173.85, 258.93) * mm, "end": v(-174.54, 259.32) * mm});
            skLineSegment(sketch, "E359", {"start": v(-180.1, 257.11) * mm, "end": v(-173.85, 258.93) * mm});
            skLineSegment(sketch, "E360", {"start": v(-179.41, 256.72) * mm, "end": v(-174.54, 258.53) * mm});
            skLineSegment(sketch, "E361", {"start": v(-179.41, 257.5) * mm, "end": v(-174.54, 259.32) * mm});
            skLineSegment(sketch, "E362", {"start": v(-179.41, 256.72) * mm, "end": v(-179.41, 217.5) * mm});
            skLineSegment(sketch, "E363", {"start": v(-174.54, 258.53) * mm, "end": v(-174.54, 217.5) * mm});
            skLineSegment(sketch, "E364", {"start": v(-148.02, 412.03) * mm, "end": v(-148.02, 438.03) * mm});
            skLineSegment(sketch, "E365", {"start": v(187, 413.37) * mm, "end": v(187, 438.03) * mm});
            skLineSegment(sketch, "E366", {"start": v(-234.68, 434.85) * mm, "end": v(273.7, 434.85) * mm});
            skLineSegment(sketch, "E367", {"start": v(100.58, -60.7) * mm, "end": v(103.63, -60.7) * mm});
            skLineSegment(sketch, "E368", {"start": v(103.63, -60.7) * mm, "end": v(103.63, -75.11) * mm});
            skLineSegment(sketch, "E369", {"start": v(100.58, -60.7) * mm, "end": v(100.58, -75.11) * mm});
            skLineSegment(sketch, "E370", {"start": v(99, -79.75) * mm, "end": v(49, -79.75) * mm});
            skLineSegment(sketch, "E371", {"start": v(99, -76.7) * mm, "end": v(49, -76.7) * mm});
            skArc(sketch, "E372", {"start": v(48.23, -75.94) * mm, "mid": v(48.45, -76.48) * mm, "end": v(49, -76.7) * mm});
            skArc(sketch, "E373", {"start": v(45.18, -75.94) * mm, "mid": v(46.3, -78.63) * mm, "end": v(49, -79.75) * mm});
            skArc(sketch, "E374", {"start": v(99, -76.7) * mm, "mid": v(100.11, -76.23) * mm, "end": v(100.58, -75.11) * mm});
            skArc(sketch, "E375", {"start": v(99, -79.75) * mm, "mid": v(102.27, -78.39) * mm, "end": v(103.63, -75.11) * mm});
            skLineSegment(sketch, "E376", {"start": v(-10.55, -60.7) * mm, "end": v(-13.6, -60.7) * mm});
            skLineSegment(sketch, "E377", {"start": v(-13.6, -60.7) * mm, "end": v(-13.6, -75.11) * mm});
            skLineSegment(sketch, "E378", {"start": v(-10.55, -60.7) * mm, "end": v(-10.55, -75.11) * mm});
            skLineSegment(sketch, "E379", {"start": v(-8.96, -79.75) * mm, "end": v(40.73, -79.75) * mm});
            skLineSegment(sketch, "E380", {"start": v(-8.96, -76.7) * mm, "end": v(40.73, -76.7) * mm});
            skArc(sketch, "E381", {"start": v(40.73, -76.7) * mm, "mid": v(41.27, -76.48) * mm, "end": v(41.5, -75.94) * mm});
            skArc(sketch, "E382", {"start": v(40.73, -79.75) * mm, "mid": v(43.43, -78.63) * mm, "end": v(44.54, -75.94) * mm});
            skArc(sketch, "E383", {"start": v(-10.55, -75.11) * mm, "mid": v(-10.08, -76.23) * mm, "end": v(-8.96, -76.7) * mm});
            skArc(sketch, "E384", {"start": v(-13.6, -75.11) * mm, "mid": v(-12.24, -78.39) * mm, "end": v(-8.96, -79.75) * mm});
            skLineSegment(sketch, "E385", {"start": v(49.63, -162.09) * mm, "end": v(187.74, -162.09) * mm});
            skLineSegment(sketch, "E386", {"start": v(187.74, -86.69) * mm, "end": v(49.63, -86.69) * mm});
            skLineSegment(sketch, "E387", {"start": v(49.63, -87.49) * mm, "end": v(187.74, -87.49) * mm});
            skLineSegment(sketch, "E388", {"start": v(187.74, -162.89) * mm, "end": v(49.63, -162.89) * mm});
            skLineSegment(sketch, "E389", {"start": v(49.63, -162.89) * mm, "end": v(49.63, -86.69) * mm});
            skLineSegment(sketch, "E390", {"start": v(40.1, -162.09) * mm, "end": v(-105.22, -162.09) * mm});
            skLineSegment(sketch, "E391", {"start": v(-105.22, -86.69) * mm, "end": v(40.1, -86.69) * mm});
            skLineSegment(sketch, "E392", {"start": v(40.1, -87.49) * mm, "end": v(-105.22, -87.49) * mm});
            skLineSegment(sketch, "E393", {"start": v(-105.22, -162.89) * mm, "end": v(40.1, -162.89) * mm});
            skLineSegment(sketch, "E394", {"start": v(40.1, -162.89) * mm, "end": v(40.1, -86.69) * mm});
            skLineSegment(sketch, "E395", {"start": v(-105.22, -164.71) * mm, "end": v(-105.22, -120.76) * mm});
            skLineSegment(sketch, "E396", {"start": v(-105.22, -115.81) * mm, "end": v(-105.22, -84.15) * mm});
            skLineSegment(sketch, "E397", {"start": v(-105.22, -120.76) * mm, "end": v(-94.08, -118.26) * mm});
            skLineSegment(sketch, "E398", {"start": v(-117.4, -118.26) * mm, "end": v(-105.22, -115.81) * mm});
            skLineSegment(sketch, "E399", {"start": v(-117.4, -118.26) * mm, "end": v(-94.08, -118.26) * mm});
            skLineSegment(sketch, "E400", {"start": v(187.74, -164.71) * mm, "end": v(187.74, -120.76) * mm});
            skLineSegment(sketch, "E401", {"start": v(187.74, -115.81) * mm, "end": v(187.74, -84.15) * mm});
            skLineSegment(sketch, "E402", {"start": v(187.74, -120.76) * mm, "end": v(198.88, -118.26) * mm});
            skLineSegment(sketch, "E403", {"start": v(175.56, -118.26) * mm, "end": v(187.74, -115.81) * mm});
            skLineSegment(sketch, "E404", {"start": v(175.56, -118.26) * mm, "end": v(198.88, -118.26) * mm});
            skLineSegment(sketch, "E405", {"start": v(-19.05, -169.3) * mm, "end": v(108.77, -169.3) * mm});
            skLineSegment(sketch, "E406", {"start": v(-18.84, -167.77) * mm, "end": v(108.57, -167.77) * mm});
            skLineSegment(sketch, "E407", {"start": v(108.57, -167.77) * mm, "end": v(119.2, -164.92) * mm});
            skLineSegment(sketch, "E408", {"start": v(108.77, -169.3) * mm, "end": v(119.6, -166.4) * mm});
            skLineSegment(sketch, "E409", {"start": v(-18.84, -167.77) * mm, "end": v(-29.47, -164.92) * mm});
            skLineSegment(sketch, "E410", {"start": v(-19.05, -169.3) * mm, "end": v(-29.87, -166.4) * mm});
            skLineSegment(sketch, "E411", {"start": v(-18.84, -81.48) * mm, "end": v(108.56, -81.48) * mm});
            skLineSegment(sketch, "E412", {"start": v(-18.64, -83) * mm, "end": v(108.36, -83) * mm});
            skLineSegment(sketch, "E413", {"start": v(108.36, -83) * mm, "end": v(119.16, -83) * mm});
            skLineSegment(sketch, "E414", {"start": v(108.16, -81.48) * mm, "end": v(119.16, -81.48) * mm});
            skLineSegment(sketch, "E415", {"start": v(-18.64, -83) * mm, "end": v(-29.43, -83) * mm});
            skLineSegment(sketch, "E416", {"start": v(-18.43, -81.48) * mm, "end": v(-29.43, -81.48) * mm});
            skLineSegment(sketch, "E417", {"start": v(187.74, -130.36) * mm, "end": v(49.63, -130.36) * mm});
            skLineSegment(sketch, "E418", {"start": v(40.1, -130.36) * mm, "end": v(-105.22, -130.36) * mm});
            skLineSegment(sketch, "E419", {"start": v(187.74, -131.16) * mm, "end": v(49.63, -131.16) * mm});
            skLineSegment(sketch, "E420", {"start": v(40.1, -131.16) * mm, "end": v(-105.22, -131.16) * mm});
            skLineSegment(sketch, "E421", {"start": v(50.63, -132.01) * mm, "end": v(152.23, -132.01) * mm});
            skLineSegment(sketch, "E422", {"start": v(50.63, -134.28) * mm, "end": v(152.23, -134.28) * mm});
            skLineSegment(sketch, "E423", {"start": v(50.63, -134.85) * mm, "end": v(152.23, -134.85) * mm});
            skLineSegment(sketch, "E424", {"start": v(50.63, -132.01) * mm, "end": v(50.63, -134.85) * mm});
            skLineSegment(sketch, "E425", {"start": v(152.23, -132.01) * mm, "end": v(152.23, -134.85) * mm});
            skLineSegment(sketch, "E426", {"start": v(-62.42, -132.01) * mm, "end": v(39.18, -132.01) * mm});
            skLineSegment(sketch, "E427", {"start": v(-62.42, -134.28) * mm, "end": v(39.18, -134.28) * mm});
            skLineSegment(sketch, "E428", {"start": v(-62.42, -134.85) * mm, "end": v(39.18, -134.85) * mm});
            skLineSegment(sketch, "E429", {"start": v(-62.42, -132.01) * mm, "end": v(-62.42, -134.85) * mm});
            skLineSegment(sketch, "E430", {"start": v(39.18, -132.01) * mm, "end": v(39.18, -134.85) * mm});
            skLineSegment(sketch, "E431", {"start": v(22.26, -136.63) * mm, "end": v(22.26, -135.36) * mm});
            skLineSegment(sketch, "E432", {"start": v(9.05, -136.63) * mm, "end": v(9.05, -135.36) * mm});
            skLineSegment(sketch, "E433", {"start": v(20.85, -141.05) * mm, "end": v(20.85, -136.63) * mm});
            skLineSegment(sketch, "E434", {"start": v(10.46, -141.05) * mm, "end": v(10.46, -136.63) * mm});
            skLineSegment(sketch, "E435", {"start": v(18.1, -93.54) * mm, "end": v(18.1, -92.52) * mm});
            skLineSegment(sketch, "E436", {"start": v(18.1, -91.73) * mm, "end": v(18.1, -90.7) * mm});
            skLineSegment(sketch, "E437", {"start": v(18.1, -89.92) * mm, "end": v(18.1, -88.9) * mm});
            skLineSegment(sketch, "E438", {"start": v(18.1, -88.1) * mm, "end": v(18.1, -87.08) * mm});
            skLineSegment(sketch, "E439", {"start": v(18.1, -86.3) * mm, "end": v(18.1, -85.27) * mm});
            skLineSegment(sketch, "E440", {"start": v(18.1, -84.48) * mm, "end": v(18.1, -83.46) * mm});
            skLineSegment(sketch, "E441", {"start": v(18.1, -82.66) * mm, "end": v(18.1, -81.64) * mm});
            skLineSegment(sketch, "E442", {"start": v(18.1, -80.85) * mm, "end": v(18.1, -79.83) * mm});
            skLineSegment(sketch, "E443", {"start": v(18.1, -75.4) * mm, "end": v(18.1, -74.39) * mm});
            skLineSegment(sketch, "E444", {"start": v(13.22, -95.36) * mm, "end": v(13.22, -94.34) * mm});
            skLineSegment(sketch, "E445", {"start": v(13.22, -93.54) * mm, "end": v(13.22, -92.52) * mm});
            skLineSegment(sketch, "E446", {"start": v(13.22, -91.73) * mm, "end": v(13.22, -90.7) * mm});
            skLineSegment(sketch, "E447", {"start": v(13.22, -89.92) * mm, "end": v(13.22, -88.9) * mm});
            skLineSegment(sketch, "E448", {"start": v(13.22, -88.1) * mm, "end": v(13.22, -87.08) * mm});
            skLineSegment(sketch, "E449", {"start": v(13.22, -86.3) * mm, "end": v(13.22, -85.27) * mm});
            skLineSegment(sketch, "E450", {"start": v(13.22, -84.48) * mm, "end": v(13.22, -83.46) * mm});
            skLineSegment(sketch, "E451", {"start": v(13.22, -82.66) * mm, "end": v(13.22, -81.64) * mm});
            skLineSegment(sketch, "E452", {"start": v(13.22, -80.85) * mm, "end": v(13.22, -79.83) * mm});
            skLineSegment(sketch, "E453", {"start": v(12.53, -93.94) * mm, "end": v(13.22, -94.34) * mm});
            skLineSegment(sketch, "E454", {"start": v(12.53, -93.94) * mm, "end": v(13.22, -93.54) * mm});
            skLineSegment(sketch, "E455", {"start": v(12.53, -92.13) * mm, "end": v(13.22, -92.52) * mm});
            skLineSegment(sketch, "E456", {"start": v(12.53, -92.13) * mm, "end": v(13.22, -91.73) * mm});
            skLineSegment(sketch, "E457", {"start": v(18.78, -92.13) * mm, "end": v(18.1, -92.52) * mm});
            skLineSegment(sketch, "E458", {"start": v(18.78, -92.13) * mm, "end": v(18.1, -91.73) * mm});
            skLineSegment(sketch, "E459", {"start": v(18.78, -90.31) * mm, "end": v(18.1, -90.7) * mm});
            skLineSegment(sketch, "E460", {"start": v(18.78, -90.31) * mm, "end": v(18.1, -89.92) * mm});
            skLineSegment(sketch, "E461", {"start": v(12.53, -93.94) * mm, "end": v(18.78, -92.13) * mm});
            skLineSegment(sketch, "E462", {"start": v(12.53, -92.13) * mm, "end": v(18.78, -90.31) * mm});
            skLineSegment(sketch, "E463", {"start": v(13.22, -94.34) * mm, "end": v(18.1, -92.52) * mm});
            skLineSegment(sketch, "E464", {"start": v(13.22, -93.54) * mm, "end": v(18.1, -91.73) * mm});
            skLineSegment(sketch, "E465", {"start": v(13.22, -92.52) * mm, "end": v(18.1, -90.7) * mm});
            skLineSegment(sketch, "E466", {"start": v(13.22, -91.73) * mm, "end": v(18.1, -89.92) * mm});
            skLineSegment(sketch, "E467", {"start": v(12.53, -90.31) * mm, "end": v(13.22, -90.7) * mm});
            skLineSegment(sketch, "E468", {"start": v(12.53, -90.31) * mm, "end": v(13.22, -89.92) * mm});
            skLineSegment(sketch, "E469", {"start": v(12.53, -88.5) * mm, "end": v(13.22, -88.9) * mm});
            skLineSegment(sketch, "E470", {"start": v(12.53, -88.5) * mm, "end": v(13.22, -88.1) * mm});
            skLineSegment(sketch, "E471", {"start": v(18.78, -88.5) * mm, "end": v(18.1, -88.9) * mm});
            skLineSegment(sketch, "E472", {"start": v(18.78, -88.5) * mm, "end": v(18.1, -88.1) * mm});
            skLineSegment(sketch, "E473", {"start": v(18.78, -86.69) * mm, "end": v(18.1, -87.08) * mm});
            skLineSegment(sketch, "E474", {"start": v(18.78, -86.69) * mm, "end": v(18.1, -86.3) * mm});
            skLineSegment(sketch, "E475", {"start": v(12.53, -90.31) * mm, "end": v(18.78, -88.5) * mm});
            skLineSegment(sketch, "E476", {"start": v(12.53, -88.5) * mm, "end": v(18.78, -86.69) * mm});
            skLineSegment(sketch, "E477", {"start": v(13.22, -90.7) * mm, "end": v(18.1, -88.9) * mm});
            skLineSegment(sketch, "E478", {"start": v(13.22, -89.92) * mm, "end": v(18.1, -88.1) * mm});
            skLineSegment(sketch, "E479", {"start": v(13.22, -88.9) * mm, "end": v(18.1, -87.08) * mm});
            skLineSegment(sketch, "E480", {"start": v(13.22, -88.1) * mm, "end": v(18.1, -86.3) * mm});
            skLineSegment(sketch, "E481", {"start": v(12.53, -86.69) * mm, "end": v(13.22, -87.08) * mm});
            skLineSegment(sketch, "E482", {"start": v(12.53, -86.69) * mm, "end": v(13.22, -86.3) * mm});
            skLineSegment(sketch, "E483", {"start": v(18.78, -84.87) * mm, "end": v(18.1, -85.27) * mm});
            skLineSegment(sketch, "E484", {"start": v(18.78, -84.87) * mm, "end": v(18.1, -84.48) * mm});
            skLineSegment(sketch, "E485", {"start": v(12.53, -86.69) * mm, "end": v(18.78, -84.87) * mm});
            skLineSegment(sketch, "E486", {"start": v(13.22, -87.08) * mm, "end": v(18.1, -85.27) * mm});
            skLineSegment(sketch, "E487", {"start": v(13.22, -86.3) * mm, "end": v(18.1, -84.48) * mm});
            skLineSegment(sketch, "E488", {"start": v(12.53, -84.87) * mm, "end": v(13.22, -85.27) * mm});
            skLineSegment(sketch, "E489", {"start": v(12.53, -84.87) * mm, "end": v(13.22, -84.48) * mm});
            skLineSegment(sketch, "E490", {"start": v(12.53, -83.06) * mm, "end": v(13.22, -83.46) * mm});
            skLineSegment(sketch, "E491", {"start": v(12.53, -83.06) * mm, "end": v(13.22, -82.66) * mm});
            skLineSegment(sketch, "E492", {"start": v(18.78, -83.06) * mm, "end": v(18.1, -83.46) * mm});
            skLineSegment(sketch, "E493", {"start": v(18.78, -83.06) * mm, "end": v(18.1, -82.66) * mm});
            skLineSegment(sketch, "E494", {"start": v(18.78, -81.25) * mm, "end": v(18.1, -81.64) * mm});
            skLineSegment(sketch, "E495", {"start": v(18.78, -81.25) * mm, "end": v(18.1, -80.85) * mm});
            skLineSegment(sketch, "E496", {"start": v(12.53, -84.87) * mm, "end": v(18.78, -83.06) * mm});
            skLineSegment(sketch, "E497", {"start": v(12.53, -83.06) * mm, "end": v(18.78, -81.25) * mm});
            skLineSegment(sketch, "E498", {"start": v(13.22, -85.27) * mm, "end": v(18.1, -83.46) * mm});
            skLineSegment(sketch, "E499", {"start": v(13.22, -84.48) * mm, "end": v(18.1, -82.66) * mm});
            skLineSegment(sketch, "E500", {"start": v(13.22, -83.46) * mm, "end": v(18.1, -81.64) * mm});
            skLineSegment(sketch, "E501", {"start": v(13.22, -82.66) * mm, "end": v(18.1, -80.85) * mm});
            skLineSegment(sketch, "E502", {"start": v(12.53, -81.25) * mm, "end": v(13.22, -81.64) * mm});
            skLineSegment(sketch, "E503", {"start": v(12.53, -81.25) * mm, "end": v(13.22, -80.85) * mm});
            skLineSegment(sketch, "E504", {"start": v(13.22, -81.64) * mm, "end": v(18.1, -79.83) * mm});
            skLineSegment(sketch, "E505", {"start": v(12.53, -75.8) * mm, "end": v(13.22, -76.2) * mm});
            skLineSegment(sketch, "E506", {"start": v(12.53, -75.8) * mm, "end": v(13.22, -75.4) * mm});
            skLineSegment(sketch, "E507", {"start": v(18.78, -75.8) * mm, "end": v(18.1, -76.2) * mm});
            skLineSegment(sketch, "E508", {"start": v(18.78, -75.8) * mm, "end": v(18.1, -75.4) * mm});
            skLineSegment(sketch, "E509", {"start": v(18.78, -74) * mm, "end": v(18.1, -74.39) * mm});
            skLineSegment(sketch, "E510", {"start": v(18.78, -74) * mm, "end": v(18.1, -73.6) * mm});
            skLineSegment(sketch, "E511", {"start": v(9.05, -135.36) * mm, "end": v(22.26, -135.36) * mm});
            skLineSegment(sketch, "E512", {"start": v(9.05, -136.63) * mm, "end": v(22.26, -136.63) * mm});
            skLineSegment(sketch, "E513", {"start": v(11.15, -141.45) * mm, "end": v(20.15, -141.45) * mm});
            skLineSegment(sketch, "E514", {"start": v(13.06, -141.05) * mm, "end": v(13.06, -136.63) * mm});
            skLineSegment(sketch, "E515", {"start": v(18.25, -141.05) * mm, "end": v(18.25, -136.63) * mm});
            skLineSegment(sketch, "E516", {"start": v(11.15, -141.45) * mm, "end": v(10.46, -141.05) * mm});
            skLineSegment(sketch, "E517", {"start": v(20.15, -141.45) * mm, "end": v(20.85, -141.05) * mm});
            skLineSegment(sketch, "E518", {"start": v(17.55, -141.45) * mm, "end": v(18.25, -141.05) * mm});
            skLineSegment(sketch, "E519", {"start": v(12.36, -141.45) * mm, "end": v(13.06, -141.05) * mm});
            skLineSegment(sketch, "E520", {"start": v(18.95, -141.45) * mm, "end": v(18.25, -141.05) * mm});
            skLineSegment(sketch, "E521", {"start": v(13.75, -141.45) * mm, "end": v(13.06, -141.05) * mm});
            skLineSegment(sketch, "E522", {"start": v(13.22, -75.4) * mm, "end": v(13.22, -63.93) * mm});
            skLineSegment(sketch, "E523", {"start": v(17.44, -73.84) * mm, "end": v(17.44, -63.93) * mm});
            skLineSegment(sketch, "E524", {"start": v(15.33, -62.7) * mm, "end": v(13.22, -63.93) * mm});
            skLineSegment(sketch, "E525", {"start": v(15.33, -62.7) * mm, "end": v(17.44, -63.93) * mm});
            skLineSegment(sketch, "E526", {"start": v(15.33, -62.7) * mm, "end": v(15.33, -72.23) * mm});
            skLineSegment(sketch, "E527", {"start": v(12.53, -95.75) * mm, "end": v(13.22, -96.15) * mm});
            skLineSegment(sketch, "E528", {"start": v(12.53, -95.75) * mm, "end": v(13.22, -95.36) * mm});
            skLineSegment(sketch, "E529", {"start": v(18.78, -93.94) * mm, "end": v(18.1, -94.34) * mm});
            skLineSegment(sketch, "E530", {"start": v(18.78, -93.94) * mm, "end": v(18.1, -93.54) * mm});
            skLineSegment(sketch, "E531", {"start": v(12.53, -95.75) * mm, "end": v(18.78, -93.94) * mm});
            skLineSegment(sketch, "E532", {"start": v(13.22, -96.15) * mm, "end": v(18.1, -94.34) * mm});
            skLineSegment(sketch, "E533", {"start": v(13.22, -95.36) * mm, "end": v(18.1, -93.54) * mm});
            skLineSegment(sketch, "E534", {"start": v(13.22, -96.15) * mm, "end": v(13.22, -135.36) * mm});
            skLineSegment(sketch, "E535", {"start": v(18.1, -94.34) * mm, "end": v(18.1, -135.36) * mm});
            skLineSegment(sketch, "E536", {"start": v(-29.43, -83) * mm, "end": v(-29.43, -81.48) * mm});
            skLineSegment(sketch, "E537", {"start": v(119.16, -83) * mm, "end": v(119.16, -81.48) * mm});
            skLineSegment(sketch, "E538", {"start": v(119.2, -164.92) * mm, "end": v(119.6, -166.4) * mm});
            skLineSegment(sketch, "E539", {"start": v(-29.87, -166.4) * mm, "end": v(-29.47, -164.92) * mm});
            skLineSegment(sketch, "E540", {"start": v(-29.16, -165.55) * mm, "end": v(2.6, -165.55) * mm});
            skLineSegment(sketch, "E541", {"start": v(-29.16, -164.03) * mm, "end": v(2.6, -164.03) * mm});
            skLineSegment(sketch, "E542", {"start": v(-29.16, -164.03) * mm, "end": v(-29.16, -165.55) * mm});
            skLineSegment(sketch, "E543", {"start": v(2.6, -164.03) * mm, "end": v(2.6, -165.55) * mm});
            skLineSegment(sketch, "E544", {"start": v(87.33, -165.55) * mm, "end": v(119.08, -165.55) * mm});
            skLineSegment(sketch, "E545", {"start": v(87.33, -164.03) * mm, "end": v(119.08, -164.03) * mm});
            skLineSegment(sketch, "E546", {"start": v(87.33, -164.03) * mm, "end": v(87.33, -165.55) * mm});
            skLineSegment(sketch, "E547", {"start": v(119.08, -164.03) * mm, "end": v(119.08, -165.55) * mm});
            skLineSegment(sketch, "E548", {"start": v(-4.94, -85.56) * mm, "end": v(34.87, -85.56) * mm});
            skLineSegment(sketch, "E549", {"start": v(-4.94, -84.04) * mm, "end": v(34.87, -84.04) * mm});
            skLineSegment(sketch, "E550", {"start": v(-4.94, -84.04) * mm, "end": v(-4.94, -85.56) * mm});
            skLineSegment(sketch, "E551", {"start": v(34.87, -84.04) * mm, "end": v(34.87, -85.56) * mm});
            skLineSegment(sketch, "E552", {"start": v(55.88, -85.56) * mm, "end": v(94.6, -85.56) * mm});
            skLineSegment(sketch, "E553", {"start": v(55.88, -84.04) * mm, "end": v(94.6, -84.04) * mm});
            skLineSegment(sketch, "E554", {"start": v(55.88, -84.04) * mm, "end": v(55.88, -85.56) * mm});
            skLineSegment(sketch, "E555", {"start": v(94.6, -84.04) * mm, "end": v(94.6, -85.56) * mm});
            skLineSegment(sketch, "E556", {"start": v(-5.7, -170.24) * mm, "end": v(-17.48, -170.24) * mm});
            skLineSegment(sketch, "E557", {"start": v(-14.28, -168.36) * mm, "end": v(-8.9, -166.58) * mm});
            skLineSegment(sketch, "E558", {"start": v(-14.28, -168.36) * mm, "end": v(-13.6, -168.75) * mm});
            skLineSegment(sketch, "E559", {"start": v(-14.28, -168.36) * mm, "end": v(-13.6, -167.97) * mm});
            skLineSegment(sketch, "E560", {"start": v(-8.9, -166.58) * mm, "end": v(-9.58, -166.19) * mm});
            skLineSegment(sketch, "E561", {"start": v(-8.9, -166.58) * mm, "end": v(-9.58, -166.97) * mm});
            skLineSegment(sketch, "E562", {"start": v(-9.58, -166.19) * mm, "end": v(-13.6, -167.97) * mm});
            skLineSegment(sketch, "E563", {"start": v(-13.6, -168.75) * mm, "end": v(-9.58, -166.97) * mm});
            skLineSegment(sketch, "E564", {"start": v(-8.9, -164.8) * mm, "end": v(-9.58, -164.4) * mm});
            skLineSegment(sketch, "E565", {"start": v(-8.9, -164.8) * mm, "end": v(-9.58, -165.2) * mm});
            skLineSegment(sketch, "E566", {"start": v(-14.28, -166.58) * mm, "end": v(-8.9, -164.8) * mm});
            skLineSegment(sketch, "E567", {"start": v(-9.58, -164.4) * mm, "end": v(-13.6, -166.19) * mm});
            skLineSegment(sketch, "E568", {"start": v(-13.6, -166.97) * mm, "end": v(-9.58, -165.2) * mm});
            skLineSegment(sketch, "E569", {"start": v(-14.28, -166.58) * mm, "end": v(-13.6, -166.97) * mm});
            skLineSegment(sketch, "E570", {"start": v(-14.28, -166.58) * mm, "end": v(-13.6, -166.19) * mm});
            skLineSegment(sketch, "E571", {"start": v(-8.9, -163.02) * mm, "end": v(-9.58, -162.63) * mm});
            skLineSegment(sketch, "E572", {"start": v(-8.9, -163.02) * mm, "end": v(-9.58, -163.42) * mm});
            skLineSegment(sketch, "E573", {"start": v(-14.28, -164.8) * mm, "end": v(-8.9, -163.02) * mm});
            skLineSegment(sketch, "E574", {"start": v(-9.58, -162.63) * mm, "end": v(-13.6, -164.4) * mm});
            skLineSegment(sketch, "E575", {"start": v(-13.6, -165.2) * mm, "end": v(-9.58, -163.42) * mm});
            skLineSegment(sketch, "E576", {"start": v(-14.28, -164.8) * mm, "end": v(-13.6, -165.2) * mm});
            skLineSegment(sketch, "E577", {"start": v(-14.28, -164.8) * mm, "end": v(-13.6, -164.4) * mm});
            skLineSegment(sketch, "E578", {"start": v(-8.9, -161.24) * mm, "end": v(-9.58, -160.85) * mm});
            skLineSegment(sketch, "E579", {"start": v(-8.9, -161.24) * mm, "end": v(-9.58, -161.64) * mm});
            skLineSegment(sketch, "E580", {"start": v(-14.28, -163.02) * mm, "end": v(-8.9, -161.24) * mm});
            skLineSegment(sketch, "E581", {"start": v(-9.58, -160.85) * mm, "end": v(-13.6, -162.63) * mm});
            skLineSegment(sketch, "E582", {"start": v(-13.6, -163.42) * mm, "end": v(-9.58, -161.64) * mm});
            skLineSegment(sketch, "E583", {"start": v(-14.28, -163.02) * mm, "end": v(-13.6, -163.42) * mm});
            skLineSegment(sketch, "E584", {"start": v(-14.28, -163.02) * mm, "end": v(-13.6, -162.63) * mm});
            skLineSegment(sketch, "E585", {"start": v(-8.9, -159.46) * mm, "end": v(-9.58, -159.07) * mm});
            skLineSegment(sketch, "E586", {"start": v(-8.9, -159.46) * mm, "end": v(-9.58, -159.86) * mm});
            skLineSegment(sketch, "E587", {"start": v(-14.28, -161.24) * mm, "end": v(-8.9, -159.46) * mm});
            skLineSegment(sketch, "E588", {"start": v(-9.58, -159.07) * mm, "end": v(-13.6, -160.85) * mm});
            skLineSegment(sketch, "E589", {"start": v(-13.6, -161.64) * mm, "end": v(-9.58, -159.86) * mm});
            skLineSegment(sketch, "E590", {"start": v(-14.28, -161.24) * mm, "end": v(-13.6, -161.64) * mm});
            skLineSegment(sketch, "E591", {"start": v(-14.28, -161.24) * mm, "end": v(-13.6, -160.85) * mm});
            skLineSegment(sketch, "E592", {"start": v(-8.9, -157.68) * mm, "end": v(-9.58, -157.29) * mm});
            skLineSegment(sketch, "E593", {"start": v(-8.9, -157.68) * mm, "end": v(-9.58, -158.08) * mm});
            skLineSegment(sketch, "E594", {"start": v(-14.28, -159.46) * mm, "end": v(-8.9, -157.68) * mm});
            skLineSegment(sketch, "E595", {"start": v(-9.58, -157.29) * mm, "end": v(-13.6, -159.07) * mm});
            skLineSegment(sketch, "E596", {"start": v(-13.6, -159.86) * mm, "end": v(-9.58, -158.08) * mm});
            skLineSegment(sketch, "E597", {"start": v(-14.28, -159.46) * mm, "end": v(-13.6, -159.86) * mm});
            skLineSegment(sketch, "E598", {"start": v(-14.28, -159.46) * mm, "end": v(-13.6, -159.07) * mm});
            skLineSegment(sketch, "E599", {"start": v(-14.28, -157.68) * mm, "end": v(-11.6, -157.19) * mm});
            skLineSegment(sketch, "E600", {"start": v(-11.6, -157.19) * mm, "end": v(-13.6, -157.29) * mm});
            skLineSegment(sketch, "E601", {"start": v(-13.6, -158.08) * mm, "end": v(-11.6, -157.19) * mm});
            skLineSegment(sketch, "E602", {"start": v(-14.28, -157.68) * mm, "end": v(-13.6, -158.08) * mm});
            skLineSegment(sketch, "E603", {"start": v(-14.28, -157.68) * mm, "end": v(-13.6, -157.29) * mm});
            skLineSegment(sketch, "E604", {"start": v(-13.6, -158.08) * mm, "end": v(-13.6, -159.07) * mm});
            skLineSegment(sketch, "E605", {"start": v(-9.58, -158.08) * mm, "end": v(-9.58, -159.07) * mm});
            skLineSegment(sketch, "E606", {"start": v(-9.58, -159.86) * mm, "end": v(-9.58, -160.85) * mm});
            skLineSegment(sketch, "E607", {"start": v(-9.58, -161.64) * mm, "end": v(-9.58, -162.63) * mm});
            skLineSegment(sketch, "E608", {"start": v(-9.58, -163.42) * mm, "end": v(-9.58, -164.4) * mm});
            skLineSegment(sketch, "E609", {"start": v(-9.58, -165.2) * mm, "end": v(-9.58, -166.19) * mm});
            skLineSegment(sketch, "E610", {"start": v(-9.58, -166.97) * mm, "end": v(-9.58, -167.97) * mm});
            skLineSegment(sketch, "E611", {"start": v(-9.58, -168.75) * mm, "end": v(-9.58, -170.24) * mm});
            skLineSegment(sketch, "E612", {"start": v(-13.6, -168.75) * mm, "end": v(-13.6, -169.74) * mm});
            skLineSegment(sketch, "E613", {"start": v(-13.6, -166.97) * mm, "end": v(-13.6, -167.97) * mm});
            skLineSegment(sketch, "E614", {"start": v(-13.6, -165.2) * mm, "end": v(-13.6, -166.19) * mm});
            skLineSegment(sketch, "E615", {"start": v(-13.6, -163.42) * mm, "end": v(-13.6, -164.4) * mm});
            skLineSegment(sketch, "E616", {"start": v(-13.6, -161.64) * mm, "end": v(-13.6, -162.63) * mm});
            skLineSegment(sketch, "E617", {"start": v(-13.6, -159.86) * mm, "end": v(-13.6, -160.85) * mm});
            skLineSegment(sketch, "E618", {"start": v(-8.9, -168.36) * mm, "end": v(-9.58, -167.97) * mm});
            skLineSegment(sketch, "E619", {"start": v(-8.9, -168.36) * mm, "end": v(-9.58, -168.75) * mm});
            skLineSegment(sketch, "E620", {"start": v(-14.28, -170.14) * mm, "end": v(-8.9, -168.36) * mm});
            skLineSegment(sketch, "E621", {"start": v(-9.58, -167.97) * mm, "end": v(-13.6, -169.74) * mm});
            skLineSegment(sketch, "E622", {"start": v(-12.93, -170.24) * mm, "end": v(-9.58, -168.75) * mm});
            skLineSegment(sketch, "E623", {"start": v(-14.28, -170.14) * mm, "end": v(-13.6, -169.74) * mm});
            skLineSegment(sketch, "E624", {"start": v(-14.28, -170.14) * mm, "end": v(-14.11, -170.24) * mm});
            skLineSegment(sketch, "E625", {"start": v(-5.7, -171.12) * mm, "end": v(-17.48, -171.12) * mm});
            skLineSegment(sketch, "E626", {"start": v(-17.48, -170.24) * mm, "end": v(-17.48, -171.12) * mm});
            skLineSegment(sketch, "E627", {"start": v(-5.7, -170.24) * mm, "end": v(-5.7, -171.12) * mm});
            skLineSegment(sketch, "E628", {"start": v(-7.92, -174.54) * mm, "end": v(-15.33, -174.54) * mm});
            skLineSegment(sketch, "E629", {"start": v(-6.75, -171.12) * mm, "end": v(-6.75, -173.47) * mm});
            skLineSegment(sketch, "E630", {"start": v(-16.43, -171.12) * mm, "end": v(-16.43, -173.47) * mm});
            skLineSegment(sketch, "E631", {"start": v(-14.16, -173.47) * mm, "end": v(-14.16, -171.12) * mm});
            skLineSegment(sketch, "E632", {"start": v(-9.03, -173.47) * mm, "end": v(-9.03, -171.12) * mm});
            skArc(sketch, "E633", {"start": v(-14.16, -173.47) * mm, "mid": v(-11.6, -174.54) * mm, "end": v(-9.03, -173.47) * mm});
            skArc(sketch, "E634", {"start": v(-9.03, -173.47) * mm, "mid": v(-7.89, -174.54) * mm, "end": v(-6.75, -173.47) * mm});
            skArc(sketch, "E635", {"start": v(-16.43, -173.47) * mm, "mid": v(-15.3, -174.54) * mm, "end": v(-14.16, -173.47) * mm});
            skLineSegment(sketch, "E636", {"start": v(-13.6, -157.29) * mm, "end": v(-13.6, -152.35) * mm});
            skLineSegment(sketch, "E637", {"start": v(-9.58, -157.29) * mm, "end": v(-9.58, -152.35) * mm});
            skLineSegment(sketch, "E638", {"start": v(-11.6, -151.19) * mm, "end": v(-13.6, -152.35) * mm});
            skLineSegment(sketch, "E639", {"start": v(-11.6, -151.19) * mm, "end": v(-9.58, -152.35) * mm});
            skLineSegment(sketch, "E640", {"start": v(-11.6, -151.19) * mm, "end": v(-11.6, -153.73) * mm});
            skArc(sketch, "E641", {"start": v(-11.6, -153.73) * mm, "mid": v(-11, -155.15) * mm, "end": v(-9.58, -155.74) * mm});
            skLineSegment(sketch, "E642", {"start": v(107.15, -170.24) * mm, "end": v(95.36, -170.24) * mm});
            skLineSegment(sketch, "E643", {"start": v(98.56, -168.36) * mm, "end": v(103.94, -166.58) * mm});
            skLineSegment(sketch, "E644", {"start": v(98.56, -168.36) * mm, "end": v(99.24, -168.75) * mm});
            skLineSegment(sketch, "E645", {"start": v(98.56, -168.36) * mm, "end": v(99.24, -167.97) * mm});
            skLineSegment(sketch, "E646", {"start": v(103.94, -166.58) * mm, "end": v(103.26, -166.19) * mm});
            skLineSegment(sketch, "E647", {"start": v(103.94, -166.58) * mm, "end": v(103.26, -166.97) * mm});
            skLineSegment(sketch, "E648", {"start": v(103.26, -166.19) * mm, "end": v(99.24, -167.97) * mm});
            skLineSegment(sketch, "E649", {"start": v(99.24, -168.75) * mm, "end": v(103.26, -166.97) * mm});
            skLineSegment(sketch, "E650", {"start": v(103.94, -164.8) * mm, "end": v(103.26, -164.4) * mm});
            skLineSegment(sketch, "E651", {"start": v(103.94, -164.8) * mm, "end": v(103.26, -165.2) * mm});
            skLineSegment(sketch, "E652", {"start": v(98.56, -166.58) * mm, "end": v(103.94, -164.8) * mm});
            skLineSegment(sketch, "E653", {"start": v(103.26, -164.4) * mm, "end": v(99.24, -166.19) * mm});
            skLineSegment(sketch, "E654", {"start": v(99.24, -166.97) * mm, "end": v(103.26, -165.2) * mm});
            skLineSegment(sketch, "E655", {"start": v(98.56, -166.58) * mm, "end": v(99.24, -166.97) * mm});
            skLineSegment(sketch, "E656", {"start": v(98.56, -166.58) * mm, "end": v(99.24, -166.19) * mm});
            skLineSegment(sketch, "E657", {"start": v(103.94, -163.02) * mm, "end": v(103.26, -162.63) * mm});
            skLineSegment(sketch, "E658", {"start": v(103.94, -163.02) * mm, "end": v(103.26, -163.42) * mm});
            skLineSegment(sketch, "E659", {"start": v(98.56, -164.8) * mm, "end": v(103.94, -163.02) * mm});
            skLineSegment(sketch, "E660", {"start": v(103.26, -162.63) * mm, "end": v(99.24, -164.4) * mm});
            skLineSegment(sketch, "E661", {"start": v(99.24, -165.2) * mm, "end": v(103.26, -163.42) * mm});
            skLineSegment(sketch, "E662", {"start": v(98.56, -164.8) * mm, "end": v(99.24, -165.2) * mm});
            skLineSegment(sketch, "E663", {"start": v(98.56, -164.8) * mm, "end": v(99.24, -164.4) * mm});
            skLineSegment(sketch, "E664", {"start": v(103.94, -161.24) * mm, "end": v(103.26, -160.85) * mm});
            skLineSegment(sketch, "E665", {"start": v(103.94, -161.24) * mm, "end": v(103.26, -161.64) * mm});
            skLineSegment(sketch, "E666", {"start": v(98.56, -163.02) * mm, "end": v(103.94, -161.24) * mm});
            skLineSegment(sketch, "E667", {"start": v(103.26, -160.85) * mm, "end": v(99.24, -162.63) * mm});
            skLineSegment(sketch, "E668", {"start": v(99.24, -163.42) * mm, "end": v(103.26, -161.64) * mm});
            skLineSegment(sketch, "E669", {"start": v(98.56, -163.02) * mm, "end": v(99.24, -163.42) * mm});
            skLineSegment(sketch, "E670", {"start": v(98.56, -163.02) * mm, "end": v(99.24, -162.63) * mm});
            skLineSegment(sketch, "E671", {"start": v(103.94, -159.46) * mm, "end": v(103.26, -159.07) * mm});
            skLineSegment(sketch, "E672", {"start": v(103.94, -159.46) * mm, "end": v(103.26, -159.86) * mm});
            skLineSegment(sketch, "E673", {"start": v(98.56, -161.24) * mm, "end": v(103.94, -159.46) * mm});
            skLineSegment(sketch, "E674", {"start": v(103.26, -159.07) * mm, "end": v(99.24, -160.85) * mm});
            skLineSegment(sketch, "E675", {"start": v(99.24, -161.64) * mm, "end": v(103.26, -159.86) * mm});
            skLineSegment(sketch, "E676", {"start": v(98.56, -161.24) * mm, "end": v(99.24, -161.64) * mm});
            skLineSegment(sketch, "E677", {"start": v(98.56, -161.24) * mm, "end": v(99.24, -160.85) * mm});
            skLineSegment(sketch, "E678", {"start": v(103.94, -157.68) * mm, "end": v(103.26, -157.29) * mm});
            skLineSegment(sketch, "E679", {"start": v(103.94, -157.68) * mm, "end": v(103.26, -158.08) * mm});
            skLineSegment(sketch, "E680", {"start": v(98.56, -159.46) * mm, "end": v(103.94, -157.68) * mm});
            skLineSegment(sketch, "E681", {"start": v(103.26, -157.29) * mm, "end": v(99.24, -159.07) * mm});
            skLineSegment(sketch, "E682", {"start": v(99.24, -159.86) * mm, "end": v(103.26, -158.08) * mm});
            skLineSegment(sketch, "E683", {"start": v(98.56, -159.46) * mm, "end": v(99.24, -159.86) * mm});
            skLineSegment(sketch, "E684", {"start": v(98.56, -159.46) * mm, "end": v(99.24, -159.07) * mm});
            skLineSegment(sketch, "E685", {"start": v(98.56, -157.68) * mm, "end": v(101.25, -157.19) * mm});
            skLineSegment(sketch, "E686", {"start": v(101.25, -157.19) * mm, "end": v(99.24, -157.29) * mm});
            skLineSegment(sketch, "E687", {"start": v(99.24, -158.08) * mm, "end": v(101.25, -157.19) * mm});
            skLineSegment(sketch, "E688", {"start": v(98.56, -157.68) * mm, "end": v(99.24, -158.08) * mm});
            skLineSegment(sketch, "E689", {"start": v(98.56, -157.68) * mm, "end": v(99.24, -157.29) * mm});
            skLineSegment(sketch, "E690", {"start": v(99.24, -158.08) * mm, "end": v(99.24, -159.07) * mm});
            skLineSegment(sketch, "E691", {"start": v(103.26, -158.08) * mm, "end": v(103.26, -159.07) * mm});
            skLineSegment(sketch, "E692", {"start": v(103.26, -159.86) * mm, "end": v(103.26, -160.85) * mm});
            skLineSegment(sketch, "E693", {"start": v(103.26, -161.64) * mm, "end": v(103.26, -162.63) * mm});
            skLineSegment(sketch, "E694", {"start": v(103.26, -163.42) * mm, "end": v(103.26, -164.4) * mm});
            skLineSegment(sketch, "E695", {"start": v(103.26, -165.2) * mm, "end": v(103.26, -166.19) * mm});
            skLineSegment(sketch, "E696", {"start": v(103.26, -166.97) * mm, "end": v(103.26, -167.97) * mm});
            skLineSegment(sketch, "E697", {"start": v(103.26, -168.75) * mm, "end": v(103.26, -170.24) * mm});
            skLineSegment(sketch, "E698", {"start": v(99.24, -168.75) * mm, "end": v(99.24, -169.74) * mm});
            skLineSegment(sketch, "E699", {"start": v(99.24, -166.97) * mm, "end": v(99.24, -167.97) * mm});
            skLineSegment(sketch, "E700", {"start": v(99.24, -165.2) * mm, "end": v(99.24, -166.19) * mm});
            skLineSegment(sketch, "E701", {"start": v(99.24, -163.42) * mm, "end": v(99.24, -164.4) * mm});
            skLineSegment(sketch, "E702", {"start": v(99.24, -161.64) * mm, "end": v(99.24, -162.63) * mm});
            skLineSegment(sketch, "E703", {"start": v(99.24, -159.86) * mm, "end": v(99.24, -160.85) * mm});
            skLineSegment(sketch, "E704", {"start": v(103.94, -168.36) * mm, "end": v(103.26, -167.97) * mm});
            skLineSegment(sketch, "E705", {"start": v(103.94, -168.36) * mm, "end": v(103.26, -168.75) * mm});
            skLineSegment(sketch, "E706", {"start": v(98.56, -170.14) * mm, "end": v(103.94, -168.36) * mm});
            skLineSegment(sketch, "E707", {"start": v(103.26, -167.97) * mm, "end": v(99.24, -169.74) * mm});
            skLineSegment(sketch, "E708", {"start": v(99.91, -170.24) * mm, "end": v(103.26, -168.75) * mm});
            skLineSegment(sketch, "E709", {"start": v(98.56, -170.14) * mm, "end": v(99.24, -169.74) * mm});
            skLineSegment(sketch, "E710", {"start": v(98.56, -170.14) * mm, "end": v(98.73, -170.24) * mm});
            skLineSegment(sketch, "E711", {"start": v(107.15, -171.12) * mm, "end": v(95.36, -171.12) * mm});
            skLineSegment(sketch, "E712", {"start": v(95.36, -170.24) * mm, "end": v(95.36, -171.12) * mm});
            skLineSegment(sketch, "E713", {"start": v(107.15, -170.24) * mm, "end": v(107.15, -171.12) * mm});
            skLineSegment(sketch, "E714", {"start": v(104.92, -174.54) * mm, "end": v(97.51, -174.54) * mm});
            skLineSegment(sketch, "E715", {"start": v(106.1, -171.12) * mm, "end": v(106.1, -173.47) * mm});
            skLineSegment(sketch, "E716", {"start": v(96.41, -171.12) * mm, "end": v(96.41, -173.47) * mm});
            skLineSegment(sketch, "E717", {"start": v(98.69, -173.47) * mm, "end": v(98.69, -171.12) * mm});
            skLineSegment(sketch, "E718", {"start": v(103.82, -173.47) * mm, "end": v(103.82, -171.12) * mm});
            skArc(sketch, "E719", {"start": v(98.69, -173.47) * mm, "mid": v(101.25, -174.54) * mm, "end": v(103.82, -173.47) * mm});
            skArc(sketch, "E720", {"start": v(103.82, -173.47) * mm, "mid": v(104.95, -174.54) * mm, "end": v(106.1, -173.47) * mm});
            skArc(sketch, "E721", {"start": v(96.41, -173.47) * mm, "mid": v(97.55, -174.54) * mm, "end": v(98.69, -173.47) * mm});
            skLineSegment(sketch, "E722", {"start": v(99.24, -157.29) * mm, "end": v(99.24, -152.35) * mm});
            skLineSegment(sketch, "E723", {"start": v(103.26, -157.29) * mm, "end": v(103.26, -152.35) * mm});
            skLineSegment(sketch, "E724", {"start": v(101.25, -151.19) * mm, "end": v(99.24, -152.35) * mm});
            skLineSegment(sketch, "E725", {"start": v(101.25, -151.19) * mm, "end": v(103.26, -152.35) * mm});
            skLineSegment(sketch, "E726", {"start": v(101.25, -151.19) * mm, "end": v(101.25, -153.73) * mm});
            skArc(sketch, "E727", {"start": v(101.25, -153.73) * mm, "mid": v(101.84, -155.15) * mm, "end": v(103.26, -155.74) * mm});
            skLineSegment(sketch, "E728", {"start": v(-9.09, 41.6) * mm, "end": v(-12.13, 41.6) * mm});
            skLineSegment(sketch, "E729", {"start": v(-12.13, 41.6) * mm, "end": v(-12.13, 56.84) * mm});
            skLineSegment(sketch, "E730", {"start": v(-9.09, 41.6) * mm, "end": v(-9.09, 56.84) * mm});
            skArc(sketch, "E731", {"start": v(-8.32, 57.6) * mm, "mid": v(-8.86, 57.38) * mm, "end": v(-9.09, 56.84) * mm});
            skArc(sketch, "E732", {"start": v(-8.32, 60.65) * mm, "mid": v(-11.02, 59.53) * mm, "end": v(-12.13, 56.84) * mm});
            skLineSegment(sketch, "E733", {"start": v(-8.32, 60.65) * mm, "end": v(40.73, 60.65) * mm});
            skLineSegment(sketch, "E734", {"start": v(-8.32, 57.6) * mm, "end": v(40.73, 57.6) * mm});
            skArc(sketch, "E735", {"start": v(41.5, 56.84) * mm, "mid": v(41.27, 57.38) * mm, "end": v(40.73, 57.6) * mm});
            skArc(sketch, "E736", {"start": v(44.54, 56.84) * mm, "mid": v(43.43, 59.53) * mm, "end": v(40.73, 60.65) * mm});
            skLineSegment(sketch, "E737", {"start": v(44.54, 56.84) * mm, "end": v(44.54, -75.94) * mm});
            skLineSegment(sketch, "E738", {"start": v(41.5, 56.84) * mm, "end": v(41.5, -75.94) * mm});
            skLineSegment(sketch, "E739", {"start": v(98.81, 41.6) * mm, "end": v(101.86, 41.6) * mm});
            skLineSegment(sketch, "E740", {"start": v(101.86, 41.6) * mm, "end": v(101.86, 56.84) * mm});
            skLineSegment(sketch, "E741", {"start": v(98.81, 41.6) * mm, "end": v(98.81, 56.84) * mm});
            skArc(sketch, "E742", {"start": v(98.81, 56.84) * mm, "mid": v(98.59, 57.38) * mm, "end": v(98.05, 57.6) * mm});
            skArc(sketch, "E743", {"start": v(101.86, 56.84) * mm, "mid": v(100.74, 59.53) * mm, "end": v(98.05, 60.65) * mm});
            skLineSegment(sketch, "E744", {"start": v(98.05, 60.65) * mm, "end": v(49, 60.65) * mm});
            skLineSegment(sketch, "E745", {"start": v(98.05, 57.6) * mm, "end": v(49, 57.6) * mm});
            skArc(sketch, "E746", {"start": v(49, 57.6) * mm, "mid": v(48.45, 57.38) * mm, "end": v(48.23, 56.84) * mm});
            skArc(sketch, "E747", {"start": v(49, 60.65) * mm, "mid": v(46.3, 59.53) * mm, "end": v(45.18, 56.84) * mm});
            skLineSegment(sketch, "E748", {"start": v(45.18, 56.84) * mm, "end": v(45.18, -75.94) * mm});
            skLineSegment(sketch, "E749", {"start": v(48.23, 56.84) * mm, "end": v(48.23, -75.94) * mm});
            skLineSegment(sketch, "E750", {"start": v(83.37, -136.63) * mm, "end": v(83.37, -135.36) * mm});
            skLineSegment(sketch, "E751", {"start": v(70.16, -136.63) * mm, "end": v(70.16, -135.36) * mm});
            skLineSegment(sketch, "E752", {"start": v(81.96, -141.05) * mm, "end": v(81.96, -136.63) * mm});
            skLineSegment(sketch, "E753", {"start": v(71.57, -141.05) * mm, "end": v(71.57, -136.63) * mm});
            skLineSegment(sketch, "E754", {"start": v(79.2, -93.54) * mm, "end": v(79.2, -92.52) * mm});
            skLineSegment(sketch, "E755", {"start": v(79.2, -91.73) * mm, "end": v(79.2, -90.7) * mm});
            skLineSegment(sketch, "E756", {"start": v(79.2, -89.92) * mm, "end": v(79.2, -88.9) * mm});
            skLineSegment(sketch, "E757", {"start": v(79.2, -88.1) * mm, "end": v(79.2, -87.08) * mm});
            skLineSegment(sketch, "E758", {"start": v(79.2, -86.3) * mm, "end": v(79.2, -85.27) * mm});
            skLineSegment(sketch, "E759", {"start": v(79.2, -84.48) * mm, "end": v(79.2, -83.46) * mm});
            skLineSegment(sketch, "E760", {"start": v(79.2, -82.66) * mm, "end": v(79.2, -81.64) * mm});
            skLineSegment(sketch, "E761", {"start": v(79.2, -80.85) * mm, "end": v(79.2, -79.83) * mm});
            skLineSegment(sketch, "E762", {"start": v(79.2, -79.04) * mm, "end": v(79.2, -78.01) * mm});
            skLineSegment(sketch, "E763", {"start": v(79.2, -77.22) * mm, "end": v(79.2, -76.2) * mm});
            skLineSegment(sketch, "E764", {"start": v(79.2, -75.4) * mm, "end": v(79.2, -74.39) * mm});
            skLineSegment(sketch, "E765", {"start": v(74.32, -95.36) * mm, "end": v(74.32, -94.34) * mm});
            skLineSegment(sketch, "E766", {"start": v(74.32, -93.54) * mm, "end": v(74.32, -92.52) * mm});
            skLineSegment(sketch, "E767", {"start": v(74.32, -91.73) * mm, "end": v(74.32, -90.7) * mm});
            skLineSegment(sketch, "E768", {"start": v(74.32, -89.92) * mm, "end": v(74.32, -88.9) * mm});
            skLineSegment(sketch, "E769", {"start": v(74.32, -88.1) * mm, "end": v(74.32, -87.08) * mm});
            skLineSegment(sketch, "E770", {"start": v(74.32, -86.3) * mm, "end": v(74.32, -85.27) * mm});
            skLineSegment(sketch, "E771", {"start": v(74.32, -84.48) * mm, "end": v(74.32, -83.46) * mm});
            skLineSegment(sketch, "E772", {"start": v(74.32, -82.66) * mm, "end": v(74.32, -81.64) * mm});
            skLineSegment(sketch, "E773", {"start": v(74.32, -80.85) * mm, "end": v(74.32, -79.83) * mm});
            skLineSegment(sketch, "E774", {"start": v(74.32, -79.04) * mm, "end": v(74.32, -78.01) * mm});
            skLineSegment(sketch, "E775", {"start": v(74.32, -77.22) * mm, "end": v(74.32, -76.2) * mm});
            skLineSegment(sketch, "E776", {"start": v(73.64, -93.94) * mm, "end": v(74.32, -94.34) * mm});
            skLineSegment(sketch, "E777", {"start": v(73.64, -93.94) * mm, "end": v(74.32, -93.54) * mm});
            skLineSegment(sketch, "E778", {"start": v(73.64, -92.13) * mm, "end": v(74.32, -92.52) * mm});
            skLineSegment(sketch, "E779", {"start": v(73.64, -92.13) * mm, "end": v(74.32, -91.73) * mm});
            skLineSegment(sketch, "E780", {"start": v(79.89, -92.13) * mm, "end": v(79.2, -92.52) * mm});
            skLineSegment(sketch, "E781", {"start": v(79.89, -92.13) * mm, "end": v(79.2, -91.73) * mm});
            skLineSegment(sketch, "E782", {"start": v(79.89, -90.31) * mm, "end": v(79.2, -90.7) * mm});
            skLineSegment(sketch, "E783", {"start": v(79.89, -90.31) * mm, "end": v(79.2, -89.92) * mm});
            skLineSegment(sketch, "E784", {"start": v(73.64, -93.94) * mm, "end": v(79.89, -92.13) * mm});
            skLineSegment(sketch, "E785", {"start": v(73.64, -92.13) * mm, "end": v(79.89, -90.31) * mm});
            skLineSegment(sketch, "E786", {"start": v(74.32, -94.34) * mm, "end": v(79.2, -92.52) * mm});
            skLineSegment(sketch, "E787", {"start": v(74.32, -93.54) * mm, "end": v(79.2, -91.73) * mm});
            skLineSegment(sketch, "E788", {"start": v(74.32, -92.52) * mm, "end": v(79.2, -90.7) * mm});
            skLineSegment(sketch, "E789", {"start": v(74.32, -91.73) * mm, "end": v(79.2, -89.92) * mm});
            skLineSegment(sketch, "E790", {"start": v(73.64, -90.31) * mm, "end": v(74.32, -90.7) * mm});
            skLineSegment(sketch, "E791", {"start": v(73.64, -90.31) * mm, "end": v(74.32, -89.92) * mm});
            skLineSegment(sketch, "E792", {"start": v(73.64, -88.5) * mm, "end": v(74.32, -88.9) * mm});
            skLineSegment(sketch, "E793", {"start": v(73.64, -88.5) * mm, "end": v(74.32, -88.1) * mm});
            skLineSegment(sketch, "E794", {"start": v(79.89, -88.5) * mm, "end": v(79.2, -88.9) * mm});
            skLineSegment(sketch, "E795", {"start": v(79.89, -88.5) * mm, "end": v(79.2, -88.1) * mm});
            skLineSegment(sketch, "E796", {"start": v(79.89, -86.69) * mm, "end": v(79.2, -87.08) * mm});
            skLineSegment(sketch, "E797", {"start": v(79.89, -86.69) * mm, "end": v(79.2, -86.3) * mm});
            skLineSegment(sketch, "E798", {"start": v(73.64, -90.31) * mm, "end": v(79.89, -88.5) * mm});
            skLineSegment(sketch, "E799", {"start": v(73.64, -88.5) * mm, "end": v(79.89, -86.69) * mm});
            skLineSegment(sketch, "E800", {"start": v(74.32, -90.7) * mm, "end": v(79.2, -88.9) * mm});
            skLineSegment(sketch, "E801", {"start": v(74.32, -89.92) * mm, "end": v(79.2, -88.1) * mm});
            skLineSegment(sketch, "E802", {"start": v(74.32, -88.9) * mm, "end": v(79.2, -87.08) * mm});
            skLineSegment(sketch, "E803", {"start": v(74.32, -88.1) * mm, "end": v(79.2, -86.3) * mm});
            skLineSegment(sketch, "E804", {"start": v(73.64, -86.69) * mm, "end": v(74.32, -87.08) * mm});
            skLineSegment(sketch, "E805", {"start": v(73.64, -86.69) * mm, "end": v(74.32, -86.3) * mm});
            skLineSegment(sketch, "E806", {"start": v(79.89, -84.87) * mm, "end": v(79.2, -85.27) * mm});
            skLineSegment(sketch, "E807", {"start": v(79.89, -84.87) * mm, "end": v(79.2, -84.48) * mm});
            skLineSegment(sketch, "E808", {"start": v(73.64, -86.69) * mm, "end": v(79.89, -84.87) * mm});
            skLineSegment(sketch, "E809", {"start": v(74.32, -87.08) * mm, "end": v(79.2, -85.27) * mm});
            skLineSegment(sketch, "E810", {"start": v(74.32, -86.3) * mm, "end": v(79.2, -84.48) * mm});
            skLineSegment(sketch, "E811", {"start": v(73.64, -84.87) * mm, "end": v(74.32, -85.27) * mm});
            skLineSegment(sketch, "E812", {"start": v(73.64, -84.87) * mm, "end": v(74.32, -84.48) * mm});
            skLineSegment(sketch, "E813", {"start": v(73.64, -83.06) * mm, "end": v(74.32, -83.46) * mm});
            skLineSegment(sketch, "E814", {"start": v(73.64, -83.06) * mm, "end": v(74.32, -82.66) * mm});
            skLineSegment(sketch, "E815", {"start": v(79.89, -83.06) * mm, "end": v(79.2, -83.46) * mm});
            skLineSegment(sketch, "E816", {"start": v(79.89, -83.06) * mm, "end": v(79.2, -82.66) * mm});
            skLineSegment(sketch, "E817", {"start": v(79.89, -81.25) * mm, "end": v(79.2, -81.64) * mm});
            skLineSegment(sketch, "E818", {"start": v(79.89, -81.25) * mm, "end": v(79.2, -80.85) * mm});
            skLineSegment(sketch, "E819", {"start": v(73.64, -84.87) * mm, "end": v(79.89, -83.06) * mm});
            skLineSegment(sketch, "E820", {"start": v(73.64, -83.06) * mm, "end": v(79.89, -81.25) * mm});
            skLineSegment(sketch, "E821", {"start": v(74.32, -85.27) * mm, "end": v(79.2, -83.46) * mm});
            skLineSegment(sketch, "E822", {"start": v(74.32, -84.48) * mm, "end": v(79.2, -82.66) * mm});
            skLineSegment(sketch, "E823", {"start": v(74.32, -83.46) * mm, "end": v(79.2, -81.64) * mm});
            skLineSegment(sketch, "E824", {"start": v(74.32, -82.66) * mm, "end": v(79.2, -80.85) * mm});
            skLineSegment(sketch, "E825", {"start": v(73.64, -81.25) * mm, "end": v(74.32, -81.64) * mm});
            skLineSegment(sketch, "E826", {"start": v(73.64, -81.25) * mm, "end": v(74.32, -80.85) * mm});
            skLineSegment(sketch, "E827", {"start": v(73.64, -79.43) * mm, "end": v(74.32, -79.83) * mm});
            skLineSegment(sketch, "E828", {"start": v(73.64, -79.43) * mm, "end": v(74.32, -79.04) * mm});
            skLineSegment(sketch, "E829", {"start": v(79.89, -79.43) * mm, "end": v(79.2, -79.83) * mm});
            skLineSegment(sketch, "E830", {"start": v(79.89, -79.43) * mm, "end": v(79.2, -79.04) * mm});
            skLineSegment(sketch, "E831", {"start": v(79.89, -77.62) * mm, "end": v(79.2, -78.01) * mm});
            skLineSegment(sketch, "E832", {"start": v(79.89, -77.62) * mm, "end": v(79.2, -77.22) * mm});
            skLineSegment(sketch, "E833", {"start": v(73.64, -81.25) * mm, "end": v(79.89, -79.43) * mm});
            skLineSegment(sketch, "E834", {"start": v(73.64, -79.43) * mm, "end": v(79.89, -77.62) * mm});
            skLineSegment(sketch, "E835", {"start": v(74.32, -81.64) * mm, "end": v(79.2, -79.83) * mm});
            skLineSegment(sketch, "E836", {"start": v(74.32, -80.85) * mm, "end": v(79.2, -79.04) * mm});
            skLineSegment(sketch, "E837", {"start": v(74.32, -79.83) * mm, "end": v(79.2, -78.01) * mm});
            skLineSegment(sketch, "E838", {"start": v(74.32, -79.04) * mm, "end": v(79.2, -77.22) * mm});
            skLineSegment(sketch, "E839", {"start": v(73.64, -77.62) * mm, "end": v(74.32, -78.01) * mm});
            skLineSegment(sketch, "E840", {"start": v(73.64, -77.62) * mm, "end": v(74.32, -77.22) * mm});
            skLineSegment(sketch, "E841", {"start": v(73.64, -75.8) * mm, "end": v(74.32, -76.2) * mm});
            skLineSegment(sketch, "E842", {"start": v(73.64, -75.8) * mm, "end": v(74.32, -75.4) * mm});
            skLineSegment(sketch, "E843", {"start": v(79.89, -75.8) * mm, "end": v(79.2, -76.2) * mm});
            skLineSegment(sketch, "E844", {"start": v(79.89, -75.8) * mm, "end": v(79.2, -75.4) * mm});
            skLineSegment(sketch, "E845", {"start": v(79.89, -74) * mm, "end": v(79.2, -74.39) * mm});
            skLineSegment(sketch, "E846", {"start": v(79.89, -74) * mm, "end": v(79.2, -73.6) * mm});
            skLineSegment(sketch, "E847", {"start": v(73.64, -77.62) * mm, "end": v(79.89, -75.8) * mm});
            skLineSegment(sketch, "E848", {"start": v(73.64, -75.8) * mm, "end": v(79.89, -74) * mm});
            skLineSegment(sketch, "E849", {"start": v(74.32, -78.01) * mm, "end": v(79.2, -76.2) * mm});
            skLineSegment(sketch, "E850", {"start": v(74.32, -77.22) * mm, "end": v(79.2, -75.4) * mm});
            skLineSegment(sketch, "E851", {"start": v(74.32, -76.2) * mm, "end": v(79.2, -74.39) * mm});
            skLineSegment(sketch, "E852", {"start": v(74.32, -75.4) * mm, "end": v(79.2, -73.6) * mm});
            skLineSegment(sketch, "E853", {"start": v(70.16, -135.36) * mm, "end": v(83.37, -135.36) * mm});
            skLineSegment(sketch, "E854", {"start": v(70.16, -136.63) * mm, "end": v(83.37, -136.63) * mm});
            skLineSegment(sketch, "E855", {"start": v(72.26, -141.45) * mm, "end": v(81.26, -141.45) * mm});
            skLineSegment(sketch, "E856", {"start": v(74.16, -141.05) * mm, "end": v(74.16, -136.63) * mm});
            skLineSegment(sketch, "E857", {"start": v(79.36, -141.05) * mm, "end": v(79.36, -136.63) * mm});
            skLineSegment(sketch, "E858", {"start": v(72.26, -141.45) * mm, "end": v(71.57, -141.05) * mm});
            skLineSegment(sketch, "E859", {"start": v(81.26, -141.45) * mm, "end": v(81.96, -141.05) * mm});
            skLineSegment(sketch, "E860", {"start": v(78.66, -141.45) * mm, "end": v(79.36, -141.05) * mm});
            skLineSegment(sketch, "E861", {"start": v(73.47, -141.45) * mm, "end": v(74.16, -141.05) * mm});
            skLineSegment(sketch, "E862", {"start": v(80.05, -141.45) * mm, "end": v(79.36, -141.05) * mm});
            skLineSegment(sketch, "E863", {"start": v(74.86, -141.45) * mm, "end": v(74.16, -141.05) * mm});
            skLineSegment(sketch, "E864", {"start": v(74.32, -75.4) * mm, "end": v(74.32, -63.93) * mm});
            skLineSegment(sketch, "E865", {"start": v(78.55, -73.84) * mm, "end": v(78.55, -63.93) * mm});
            skLineSegment(sketch, "E866", {"start": v(76.44, -62.7) * mm, "end": v(74.32, -63.93) * mm});
            skLineSegment(sketch, "E867", {"start": v(76.44, -62.7) * mm, "end": v(78.55, -63.93) * mm});
            skLineSegment(sketch, "E868", {"start": v(76.44, -62.7) * mm, "end": v(76.44, -72.23) * mm});
            skArc(sketch, "E869", {"start": v(76.44, -72.23) * mm, "mid": v(76.77, -73.38) * mm, "end": v(77.68, -74.16) * mm});
            skLineSegment(sketch, "E870", {"start": v(73.64, -95.75) * mm, "end": v(74.32, -96.15) * mm});
            skLineSegment(sketch, "E871", {"start": v(73.64, -95.75) * mm, "end": v(74.32, -95.36) * mm});
            skLineSegment(sketch, "E872", {"start": v(79.89, -93.94) * mm, "end": v(79.2, -94.34) * mm});
            skLineSegment(sketch, "E873", {"start": v(79.89, -93.94) * mm, "end": v(79.2, -93.54) * mm});
            skLineSegment(sketch, "E874", {"start": v(73.64, -95.75) * mm, "end": v(79.89, -93.94) * mm});
            skLineSegment(sketch, "E875", {"start": v(74.32, -96.15) * mm, "end": v(79.2, -94.34) * mm});
            skLineSegment(sketch, "E876", {"start": v(74.32, -95.36) * mm, "end": v(79.2, -93.54) * mm});
            skLineSegment(sketch, "E877", {"start": v(74.32, -96.15) * mm, "end": v(74.32, -135.36) * mm});
            skLineSegment(sketch, "E878", {"start": v(79.2, -94.34) * mm, "end": v(79.2, -135.36) * mm});
            skSolve(sketch);
        }
        {
            var Q0;
            Q0=makeQuery(id+"F0.imprint","IMPRINT",FACE,{"disambiguationData":[TD([[makeQuery(id+"F0.imprint","IMPRINT",EDGE,{"derivedFrom":sQuery(id+"F0.wireOp",EDGE,"E376")}),1.0]])]});
            extrude(context, id + "F1", {"entities" : qUnion([Q0]), "depth" : 2438.4 * mm});
        }
        {
            var Q0;
            Q0=makeQuery(id+"F1.opExtrude","SWEPT_FACE",FACE,{"disambiguationData":[OSD([sQuery(id+"F0.wireOp",EDGE,"E733")])]});
            var sketch = newSketch(context, id + "F2", { "sketchPlane" : qUnion([Q0])});
            skLineSegment(sketch, "E879.bottom", {"start": v(-56.27, -2461.53) * mm, "end": v(92.9, -2461.53) * mm});
            skLineSegment(sketch, "E879.top", {"start": v(-56.27, -2331.98) * mm, "end": v(92.9, -2331.98) * mm});
            skLineSegment(sketch, "E879.left", {"start": v(-56.27, -2461.53) * mm, "end": v(-56.27, -2331.98) * mm});
            skLineSegment(sketch, "E879.right", {"start": v(92.9, -2461.53) * mm, "end": v(92.9, -2331.98) * mm});
            skLineSegment(sketch, "E880.bottom", {"start": v(-56.28, 23.14) * mm, "end": v(92.9, 23.14) * mm});
            skLineSegment(sketch, "E880.top", {"start": v(-56.28, -106.41) * mm, "end": v(92.9, -106.41) * mm});
            skLineSegment(sketch, "E880.left", {"start": v(-56.28, 23.14) * mm, "end": v(-56.28, -106.41) * mm});
            skLineSegment(sketch, "E880.right", {"start": v(92.9, 23.14) * mm, "end": v(92.9, -106.41) * mm});
            skSolve(sketch);
        }
        {
            var Q0;
            Q0=makeQuery(id+"F2.imprint","IMPRINT",FACE,{"disambiguationData":[TD([[makeQuery(id+"F2.imprint","IMPRINT",EDGE,{"derivedFrom":sQuery(id+"F2.wireOp",EDGE,"E880.bottom")}),-1.0]])]});
            var Q1;
            {var subQ1=sQuery(id+"F0.wireOp",EDGE,"E733");var subQ6=makeQuery(id+"F1.opExtrude","CAP_EDGE",EDGE,{"disambiguationData":[OSD([subQ1])],"isStart":true});Q1=makeQuery(id+"F2.imprint","IMPRINT",FACE,{"disambiguationData":[TD([[makeQuery(id+"F2.imprint","IMPRINT",EDGE,{"derivedFrom":subQ6}),-1.0]])]});}
            extrude(context, id + "F3", {"entities" : qUnion([Q0, Q1]), "operationType" : NewBodyOperationType.REMOVE, "endBound" : BoundingType.THROUGH_ALL, "oppositeDirection" : true, "depth" : 25.4 * mm});
        }
        {
            var Q0;
            Q0=makeQuery(id+"F1.opExtrude","SWEPT_FACE",FACE,{"disambiguationData":[OSD([sQuery(id+"F0.wireOp",EDGE,"E733")])]});
            var sketch = newSketch(context, id + "F4", { "sketchPlane" : qUnion([Q0])});
            skLineSegment(sketch, "E881", {"start": v(40.73, -2438.4) * mm, "end": v(40.73, -1954.6) * mm});
            skLineSegment(sketch, "E882", {"start": v(40.73, -1954.6) * mm, "end": v(16.2, -1954.6) * mm});
            skPoint(sketch, "E882.endSnap0", {"position": v(16.2, -2438.4) * mm});
            skCircle(sketch, "E883", {"center": v(16.2, -1954.6) * mm, "radius": 3.18 * mm});
            skCircle(sketch, "E884.0.1.0", {"center": v(16.2, -1499.54) * mm, "radius": 3.18 * mm});
            skCircle(sketch, "E884.0.2.0", {"center": v(16.2, -1044.47) * mm, "radius": 3.18 * mm});
            skCircle(sketch, "E884.0.3.0", {"center": v(16.2, -589.4) * mm, "radius": 3.18 * mm});
            skCircle(sketch, "E884.0.4.0", {"center": v(16.2, -134.34) * mm, "radius": 3.18 * mm});
            skLineSegment(sketch, "E884.direction1", {"start": v(16.2, -1954.6) * mm, "end": v(41.6, -1954.6) * mm, "construction": true});
            skLineSegment(sketch, "E884.direction2", {"start": v(16.2, -1954.6) * mm, "end": v(16.2, -1499.54) * mm, "construction": true});
            skSolve(sketch);
        }
        {
            var Q0;
            Q0=makeQuery(id+"F4.imprint","IMPRINT",FACE,{"disambiguationData":[TD([[makeQuery(id+"F4.imprint","IMPRINT",EDGE,{"derivedFrom":sQuery(id+"F4.wireOp",EDGE,"E884.0.4.0")}),1.0]])]});
            var Q1;
            Q1=makeQuery(id+"F4.imprint","IMPRINT",FACE,{"disambiguationData":[TD([[makeQuery(id+"F4.imprint","IMPRINT",EDGE,{"derivedFrom":sQuery(id+"F4.wireOp",EDGE,"E884.0.3.0")}),1.0]])]});
            var Q2;
            Q2=makeQuery(id+"F4.imprint","IMPRINT",FACE,{"disambiguationData":[TD([[makeQuery(id+"F4.imprint","IMPRINT",EDGE,{"derivedFrom":sQuery(id+"F4.wireOp",EDGE,"E884.0.2.0")}),1.0]])]});
            var Q3;
            Q3=makeQuery(id+"F4.imprint","IMPRINT",FACE,{"disambiguationData":[TD([[makeQuery(id+"F4.imprint","IMPRINT",EDGE,{"derivedFrom":sQuery(id+"F4.wireOp",EDGE,"E884.0.1.0")}),1.0]])]});
            var Q4;
            Q4=makeQuery(id+"F4.imprint","IMPRINT",FACE,{"disambiguationData":[TD([[makeQuery(id+"F4.imprint","IMPRINT",EDGE,{"derivedFrom":sQuery(id+"F4.wireOp",EDGE,"E883")}),1.0]])]});
            extrude(context, id + "F5", {"entities" : qUnion([Q0, Q1, Q2, Q3, Q4]), "operationType" : NewBodyOperationType.REMOVE, "oppositeDirection" : true, "depth" : 3.3 * mm});
        }
    });
